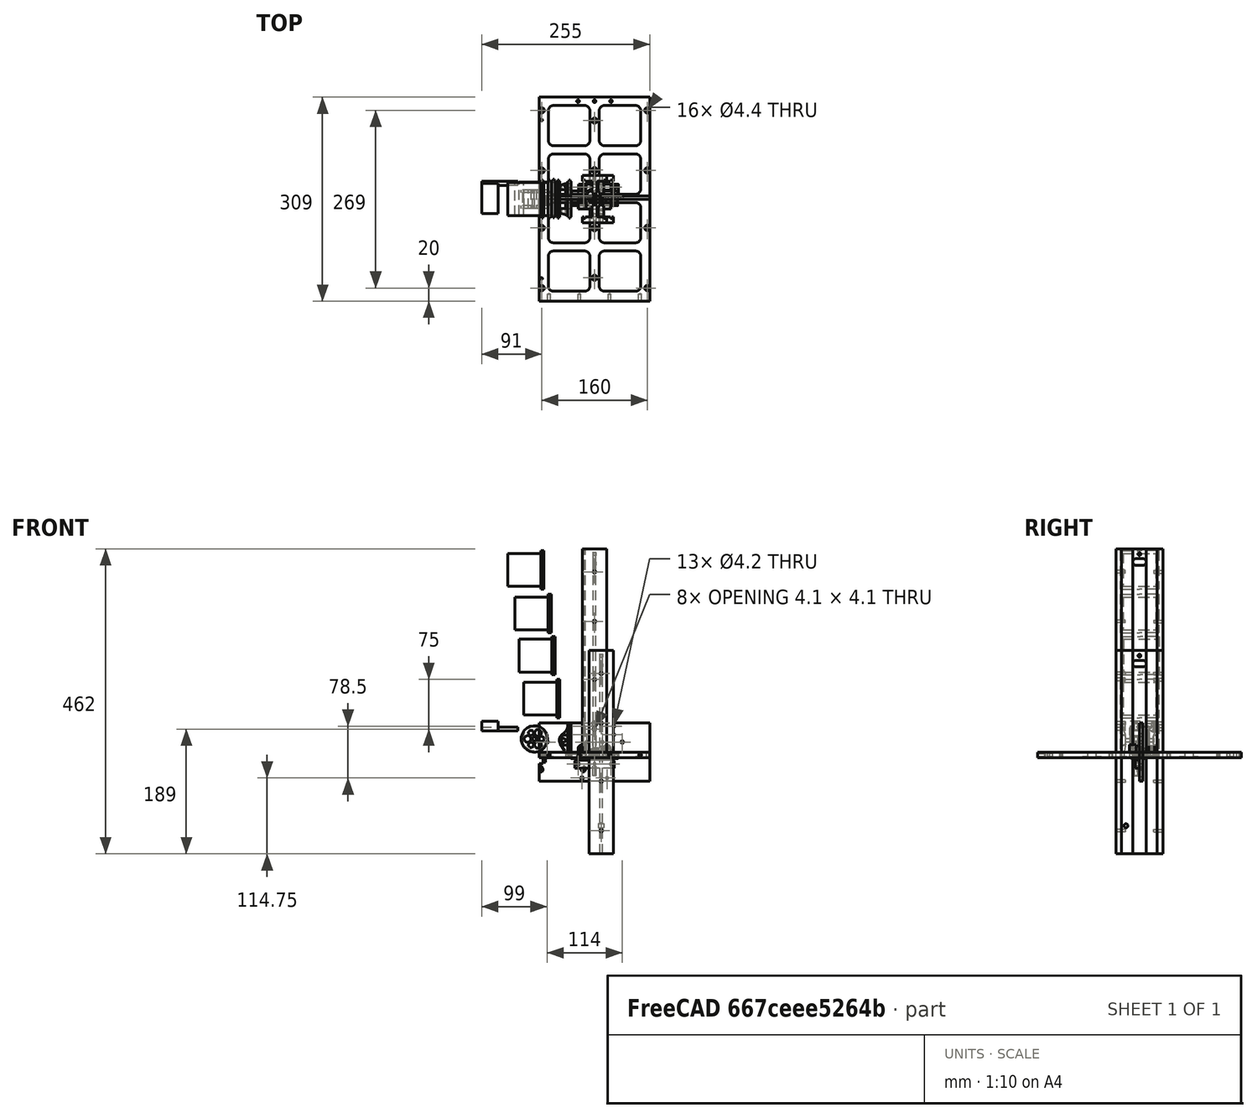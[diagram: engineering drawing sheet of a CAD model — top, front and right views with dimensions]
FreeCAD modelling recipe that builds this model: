
FCSTD DOCUMENT  (FreeCAD 0.22R35966 (Git))
Label: simulation
License: CreativeCommons Attribution-ShareAlike
LicenseURL: http://creativecommons.org/licenses/by-sa/4.0/
objects: PartDesign::CoordinateSystem×63, App::DocumentObjectGroupPython×56, Part::FeaturePython×21, App::Part×17, App::MaterialObjectPython×8, App::Link×7, App::DocumentObjectGroup×3, Part::Feature×3, App::TextDocument×3, Part::Line×3, App::FeaturePython×3
note: 90 computed .brp shape members not serialized (recipe doc carries the construction recipe); baked Part::Feature solids carry a one-line shape summary decoded from their .brp
EXTERNAL_REF file=pusher.FCStd obj=Part
EXTERNAL_REF file=pocketqube.FCStd obj=Part
EXTERNAL_REF file=pusher.FCStd obj=Part001
EXTERNAL_REF file=Stopper.FCStd obj=Part

FEATURE [Part::FeaturePython] rail_001  # a2plus imported part (geometry in sourceFile) (typed FeaturePython)
  Placement = pos=(6,0,0) rot=(0,0,1;0rad)
  a2p_Version = V0.1
  fixedPosition = false
  objectType = a2pPart
  sourceFile = ./rail.FCStd
  subassemblyImport = false
  timeLastImport = 1.5734e+09
  updateColors = true
FEATURE [App::Part] Part  label="Rail"
  Group = -> [rail_001]
  Origin = -> Origin
  Placement = pos=(10,0,154) rot=(0,0,-1;3.14159rad)
FEATURE [App::Link] Link003  label="PusherR"
  LinkPlacement = pos=(-27,-5.126e-06,43) rot=(0.57735,-0.57735,-0.57735;2.0944rad)
  LinkedObject = -> <external pusher.FCStd>#Part
  Placement = pos=(-27,-5.126e-06,43) rot=(0.57735,-0.57735,-0.57735;2.0944rad)
FEATURE [App::Link] Link  label="Satellite4R"
  LinkPlacement = pos=(-55,3.09944e-06,81) rot=(0,1,0;3.14159rad)
  LinkedObject = -> <external pocketqube.FCStd>#Part
  Placement = pos=(-55,3.09944e-06,81) rot=(0,1,0;3.14159rad)
FEATURE [App::Link] Link004  label="Satellite3R"
  LinkPlacement = pos=(-62,1.00001,146) rot=(0,1,0;3.14159rad)
  LinkedObject = -> <external pocketqube.FCStd>#Part
  Placement = pos=(-62,1.00001,146) rot=(0,1,0;3.14159rad)
FEATURE [App::Link] Link005  label="Satellite2R"
  LinkPlacement = pos=(-68,1.69277e-05,210) rot=(0,1,0;3.14159rad)
  LinkedObject = -> <external pocketqube.FCStd>#Part
  Placement = pos=(-68,1.69277e-05,210) rot=(0,1,0;3.14159rad)
FEATURE [App::Link] Link006  label="Satellite1R"
  LinkPlacement = pos=(-79,3.29018e-05,276) rot=(0,1,0;3.14159rad)
  LinkedObject = -> <external pocketqube.FCStd>#Part
  Placement = pos=(-79,3.29018e-05,276) rot=(0,1,0;3.14159rad)
FEATURE [Part::FeaturePython] Point001  # WARN: FeaturePython — macro-defined, semantics opaque (R4)
  Placement = pos=(-131.45,3.15905e-05,240) rot=(0,0,1;0rad)
  X = -131.45
  Y = 3.15905e-05
  Z = 240
FEATURE [Part::FeaturePython] Point002  # WARN: FeaturePython — macro-defined, semantics opaque (R4)
  Placement = pos=(-120.45,1.58548e-05,226) rot=(0,0,1;0rad)
  X = -120.45
  Y = 1.58548e-05
  Z = 226
FEATURE [App::Part] Part001  label="ContactPointSatellite1"
  Group = -> [Point001]
  Origin = -> Origin005
  Placement = pos=(-26,0,0) rot=(0,0,1;0rad)
FEATURE [App::Part] Part002  label="ContactPointSatellite2_1"
  Group = -> [Point002]
  Origin = -> Origin006
  Placement = pos=(-21,0,0) rot=(0,0,1;0rad)
FEATURE [Part::FeaturePython] Point  # WARN: FeaturePython — macro-defined, semantics opaque (R4)
  Placement = pos=(-120.45,1.58548e-05,176) rot=(0,0,1;0rad)
  X = -120.45
  Y = 1.58548e-05
  Z = 176
FEATURE [Part::FeaturePython] Point003  # WARN: FeaturePython — macro-defined, semantics opaque (R4)
  Placement = pos=(-114.45,1.00001,166) rot=(0,0,1;0rad)
  X = -114.45
  Y = 1.00001
  Z = 166
FEATURE [App::Part] Part003  label="ContactPointSatellite3_1"
  Group = -> [Point003]
  Origin = -> Origin007
  Placement = pos=(-13,0,0) rot=(0,0,1;0rad)
FEATURE [App::Part] Part004  label="ContactPointSatellite2_002"
  Group = -> [Point]
  Origin = -> Origin008
  Placement = pos=(-13,0,0) rot=(0,0,1;0rad)
FEATURE [Part::FeaturePython] Point004  # WARN: FeaturePython — macro-defined, semantics opaque (R4)
  Placement = pos=(-114.45,1.00001,116) rot=(0,0,1;0rad)
  X = -114.45
  Y = 1.00001
  Z = 116
FEATURE [Part::FeaturePython] Point005  # WARN: FeaturePython — macro-defined, semantics opaque (R4)
  Placement = pos=(-107.45,3.09944e-06,106) rot=(0,0,1;0rad)
  X = -107.45
  Y = 3.09944e-06
  Z = 106
FEATURE [App::Part] Part005
  Group = -> [Point004]
  Origin = -> Origin009
  Placement = pos=(-10,0,0) rot=(0,0,1;0rad)
FEATURE [App::Part] Part006
  Group = -> [Point005]
  Origin = -> Origin010
  Placement = pos=(-10,0,0) rot=(0,0,1;0rad)
FEATURE [App::DocumentObjectGroup] Group001  label="ContactPoints"
  Group = -> [Part001,Part002,Part003,Part004,Part005,Part006]
FEATURE [App::Link] Link007  label="Spool"
  LinkPlacement = pos=(-66,1.1146e-05,0) rot=(0,0,-1;1.5708rad)
  LinkedObject = -> <external pusher.FCStd>#Part001
  Placement = pos=(-66,1.1146e-05,0) rot=(0,0,-1;1.5708rad)
FEATURE [Part::Feature] y_plate_002  label="y-plate_002"
  shape: bbox 168 x 309 x 8.5 mm, 116 faces (baked)
FEATURE [App::Part] Part007  label="y-plate-up"
  Group = -> [y_plate_002]
  Origin = -> Origin011
  Placement = pos=(0,-88,132) rot=(1,0,0;1.5708rad)
FEATURE [Part::Feature] door_002
  shape: bbox 60 x 6 x 33.5 mm, 39 faces (baked)
FEATURE [App::Part] Part008  label="DoorLock"
  Group = -> [door_002]
  Origin = -> Origin012
  Placement = pos=(0,-104,304) rot=(0,0,1;3.14159rad)
FEATURE [Part::Feature] y_plate_001002  label="y-plate_003"
  shape: bbox 168 x 309 x 8.5 mm, 116 faces (baked)
FEATURE [App::Part] Part009  label="y-plate-down"
  Group = -> [y_plate_001002]
  Origin = -> Origin013
  Placement = pos=(0,122,142) rot=(0,0.707107,0.707107;3.14159rad)
FEATURE [Part::FeaturePython] hinge_002  # a2plus imported part (geometry in sourceFile) (typed FeaturePython)
  a2p_Version = V0.1
  fixedPosition = false
  objectType = a2pPart
  sourceFile = ./hinge.FCStd
  sourcePart = StatikHinge
  subassemblyImport = false
  timeLastImport = 1.58453e+09
  updateColors = true
FEATURE [App::Part] Part010  label="DoorHingeHolder"
  Group = -> [hinge_002]
  Origin = -> Origin014
  Placement = pos=(4.69e-14,160,299) rot=(0,-0.707107,0.707107;3.14159rad)
FEATURE [Part::FeaturePython] hinge_001  # a2plus imported part (geometry in sourceFile) (typed FeaturePython)
  a2p_Version = V0.1
  fixedPosition = false
  sourceFile = ./hinge.FCStd
  sourcePart = DoorHinge
  subassemblyImport = false
  timeLastImport = 1.57919e+09
  updateColors = true
FEATURE [App::Part] Part011  label="Hinge"
  Group = -> [hinge_001]
  Origin = -> Origin015
  Placement = pos=(1.93e-14,158,328) rot=(0,0.707107,-0.707107;3.14159rad)
FEATURE [Part::FeaturePython] door_001  # a2plus imported part (geometry in sourceFile) (typed FeaturePython)
  a2p_Version = V0.1
  fixedPosition = true
  sourceFile = ./door.FCStd
  sourcePart = Door
  subassemblyImport = false
  timeLastImport = 1.57919e+09
  updateColors = true
FEATURE [App::Part] Part012  label="Door"
  Group = -> [door_001]
  Origin = -> Origin016
  Placement = pos=(0,-5.8e-15,390) rot=(0,-0.707107,0.707107;3.14159rad)
FEATURE [Part::FeaturePython] door_003  # a2plus imported part (geometry in sourceFile) (typed FeaturePython)
  a2p_Version = V0.1
  fixedPosition = false
  sourceFile = ./door.FCStd
  sourcePart = BushingHolder
  subassemblyImport = false
  timeLastImport = 1.57919e+09
  updateColors = true
FEATURE [App::Part] Part013  label="DoorSlider"
  Group = -> [door_003]
  Origin = -> Origin017
  Placement = pos=(2.9e-15,-15,429) rot=(0,0,1;3.14159rad)
FEATURE [Part::FeaturePython] door_005  # a2plus imported part (geometry in sourceFile) (typed FeaturePython)
  a2p_Version = V0.1
  fixedPosition = false
  sourceFile = ./door.FCStd
  sourcePart = Slider
  subassemblyImport = false
  timeLastImport = 1.57919e+09
  updateColors = true
FEATURE [Part::FeaturePython] door_004  # a2plus imported part (geometry in sourceFile) (typed FeaturePython)
  a2p_Version = V0.1
  fixedPosition = false
  sourceFile = ./door.FCStd
  sourcePart = Pin
  subassemblyImport = false
  timeLastImport = 1.57919e+09
  updateColors = true
FEATURE [App::Part] Part014  label="DoorShaft"
  Group = -> [door_004]
  Origin = -> Origin018
  Placement = pos=(0,30,423) rot=(1,0,0;4.71239rad)
FEATURE [App::Part] Part015  label="DooShaftPusher"
  Group = -> [door_005]
  Origin = -> Origin019
  Placement = pos=(0,86,429) rot=(1,0,0;1.5708rad)
FEATURE [App::DocumentObjectGroupPython] MBD_animated_vectors  # scripted group (container) (typed FeaturePython)
FEATURE [App::DocumentObjectGroupPython] MBD_constitutive_laws  # scripted group (container) (typed FeaturePython)
FEATURE [App::DocumentObjectGroupPython] MBD_abstract_nodes  # scripted group (container) (typed FeaturePython)
FEATURE [App::DocumentObjectGroupPython] MBD_hydraulic_nodes  # scripted group (container) (typed FeaturePython)
FEATURE [App::DocumentObjectGroupPython] MBD_structural_static_nodes  # scripted group (container) (typed FeaturePython)
FEATURE [App::DocumentObjectGroupPython] MBD_beam_elements  # scripted group (container) (typed FeaturePython)
FEATURE [App::DocumentObjectGroupPython] MBD_genel_clamps  # scripted group (container) (typed FeaturePython)
FEATURE [App::DocumentObjectGroupPython] MBD_genel_elements  # scripted group (container) (typed FeaturePython)
  Group = -> [MBD_genel_clamps]
FEATURE [App::DocumentObjectGroupPython] MBD_gravity_elements  # scripted group (container) (typed FeaturePython)
FEATURE [App::DocumentObjectGroupPython] MBD_hydraulic_fluid_elements  # scripted group (container) (typed FeaturePython)
FEATURE [App::DocumentObjectGroupPython] MBD_hydraulic_elements  # scripted group (container) (typed FeaturePython)
  Group = -> [MBD_hydraulic_fluid_elements]
FEATURE [App::DocumentObjectGroupPython] MBD_angular_acceleration_joints  # scripted group (container) (typed FeaturePython)
FEATURE [App::DocumentObjectGroupPython] MBD_angular_velocity_joints  # scripted group (container) (typed FeaturePython)
FEATURE [App::DocumentObjectGroupPython] MBD_assembly_joints  # scripted group (container) (typed FeaturePython)
FEATURE [App::DocumentObjectGroupPython] MBD_coincidence_joints  # scripted group (container) (typed FeaturePython)
FEATURE [App::DocumentObjectGroupPython] MBD_cylindrical_joints  # scripted group (container) (typed FeaturePython)
FEATURE [App::DocumentObjectGroupPython] MBD_deformable_axial_joints  # scripted group (container) (typed FeaturePython)
FEATURE [App::DocumentObjectGroupPython] MBD_deformable_displacement_joints  # scripted group (container) (typed FeaturePython)
FEATURE [App::DocumentObjectGroupPython] MBD_deformable_hinge_joints  # scripted group (container) (typed FeaturePython)
FEATURE [App::DocumentObjectGroupPython] MBD_distance_joints  # scripted group (container) (typed FeaturePython)
FEATURE [App::DocumentObjectGroupPython] MBD_drive_hinge_joints  # scripted group (container) (typed FeaturePython)
FEATURE [App::DocumentObjectGroupPython] MBD_in_line_joints  # scripted group (container) (typed FeaturePython)
FEATURE [App::DocumentObjectGroupPython] MBD_linear_acceleration_joints  # scripted group (container) (typed FeaturePython)
FEATURE [App::DocumentObjectGroupPython] MBD_linear_velocity_joints  # scripted group (container) (typed FeaturePython)
FEATURE [App::DocumentObjectGroupPython] MBD_prismatic_joints  # scripted group (container) (typed FeaturePython)
FEATURE [App::DocumentObjectGroupPython] MBD_revolute_pin_joints  # scripted group (container) (typed FeaturePython)
FEATURE [App::DocumentObjectGroupPython] MBD_revolute_rotation_joints  # scripted group (container) (typed FeaturePython)
FEATURE [App::DocumentObjectGroupPython] MBD_shock_absorber_joints  # scripted group (container) (typed FeaturePython)
FEATURE [App::DocumentObjectGroupPython] MBD_spherical_hinge_joints  # scripted group (container) (typed FeaturePython)
FEATURE [App::DocumentObjectGroupPython] MBD_total_joints  # scripted group (container) (typed FeaturePython)
FEATURE [App::DocumentObjectGroupPython] MBD_total_pin_joints  # scripted group (container) (typed FeaturePython)
FEATURE [App::DocumentObjectGroupPython] MBD_viscous_body_joints  # scripted group (container) (typed FeaturePython)
FEATURE [App::DocumentObjectGroupPython] MBD_dummy_body_elements  # scripted group (container) (typed FeaturePython)
FEATURE [App::DocumentObjectGroupPython] MBD_gear_body_elements  # scripted group (container) (typed FeaturePython)
FEATURE [App::DocumentObjectGroupPython] MBD_static_body_elements  # scripted group (container) (typed FeaturePython)
FEATURE [App::DocumentObjectGroupPython] MBD_structural_couple_elements  # scripted group (container) (typed FeaturePython)
FEATURE [App::DocumentObjectGroupPython] MBD_scalar_functions  # scripted group (container) (typed FeaturePython)
FEATURE [App::TextDocument] ELEMENT_input_file
  Text = <blob: 59088 chars omitted>
FEATURE [App::TextDocument] ELEMENT_input_file_aux
  Text = begin: data;\n     problem: initial value;\n end: data;\n\n set: real XL = 0.0;\n set: real XU = 4.0;\n set: real dX = 0.01;\n\n begin: initial value;\n     initial time:   XL;\n     final time:     XU;\n     time step:      dX;\n     max iterations: 10;\n     tolerance:      1.e-6;\n     derivatives coefficient: auto;\n end: initial value;\n\n begin: control data;\n     abstract nodes: 2;\n     genels: 2;\n end: control data;\n\n     drive caller: 1, name, "drive: 1 ", cosine, 0.0, 3.1416, 7.0, half, 0.0;\n\n set: integer NoAbs_X = 1;\n set: integer NoAbs_Y = 2;\n set: integer GeClamp_NoAbs_X = 1;\n set: integer GeClamp_NoAbs_Y = 2;\n\n begin: nodes;\n     abstract: NoAbs_X, algebraic, value, XL;\n     abstract: NoAbs_Y, algebraic, value, model::drive(1, Time);\n end: nodes;\n\n set: [dof, X, NoAbs_X, abstract, algebraic];\n\n begin: elements;\n     genel: GeClamp_NoAbs_X,\n         clamp,\n         NoAbs_X, abstract,\n         string, "Time+XL";\n\n     genel: GeClamp_NoAbs_Y,\n         clamp,\n         NoAbs_Y, abstract,\n         string, "model::drive(1, Time)";\n\n end: elements;
FEATURE [App::DocumentObjectGroupPython] MBD_input_files  # scripted group (container) (typed FeaturePython)
  Group = -> [ELEMENT_input_file,ELEMENT_input_file_aux]
FEATURE [App::TextDocument] ELEMENT_variables
FEATURE [App::DocumentObjectGroupPython] MBD_user_defined_variables  # scripted group (container) (typed FeaturePython)
  Group = -> [ELEMENT_variables]
FEATURE [Part::Line] ELEMENT_cmx
  AttacherType = Attacher::AttachEngine3D
  X1 = -55
  X2 = -89.45
  Y1 = 3.09944e-06
  Y2 = 1.00001
  Z1 = 110
  Z2 = 121
FEATURE [Part::Line] ELEMENT_cmy
  AttacherType = Attacher::AttachEngine3D
  X1 = 0
  X2 = 0
  Y1 = 0
  Y2 = 0
  Z1 = 0
  Z2 = 1
FEATURE [Part::Line] ELEMENT_cmz
  AttacherType = Attacher::AttachEngine3D
  X1 = 0
  X2 = 0
  Y1 = 0
  Y2 = 0
  Z1 = 0
  Z2 = 1
FEATURE [PartDesign::CoordinateSystem] ELEMENT_ground
  AttacherType = Attacher::AttachEngine3D
FEATURE [App::DocumentObjectGroupPython] MBD_global_reference_frame  # scripted group (container) (typed FeaturePython)
  Group = -> [ELEMENT_cmx,ELEMENT_cmy,ELEMENT_cmz,ELEMENT_ground]
FEATURE [App::FeaturePython] ELEMENT_parameters  # WARN: FeaturePython — macro-defined, semantics opaque (R4)
  assembly_max_iterations = 1000
  default_orientation = 0
  derivatives_coefficient = auto
  derivatives_max_iterations = 100
  derivatives_tolerance = 0.0001
  final_time = 1
  initial_position_stiffness = 1
  initial_time = 0
  initial_velocity_stiffness = 1
  integration_max_iterations = 100
  model = 0
  modules_to_load = 0
  omega_rotates = 0
  output_data = 0
  output_meter = 10
  path_to_ELEMENT_executable = <userpath>/.local/share/FreeCAD/Mod/FreeCAD-motion-workbench-master/mbdyn-1.7.3-executables/LinuxExecutable/mbdyn
  print = 0
  skip_initial_joint_assembly = 0
  solver = 0
  time_step = 0.0001
  tolerance = 1e-06
  type_of_path_to_ELEMENT_executable = 0
  type_of_path_to_run_time_loadable_modules = 0
  type_of_working_directory = 0
  units = 0
FEATURE [App::FeaturePython] ELEMENT_animation  # WARN: FeaturePython — macro-defined, semantics opaque (R4)
  animationClicked = false
  assembled = false
  association0 = none
  association1 = none
  association2 = none
  association3 = none
  association4 = none
  association5 = none
  association6 = none
  association7 = none
  association8 = none
  association9 = none
  bodies_line_width = 1
  bodies_point_size = 4
  characteristic_length = 657
  continous = true
  current_time = 0
  current_time_step = 0
  follow_selected_object = false
  highlight_element = true
  objects_to_animate = 0
  speed = 0
  stop_at_time = 0
  stop_at_time_step = 0
  subAssembly = true
  transparency_when_assembled = 0
  transparency_when_exploded = 50
  zoon_when_contracted = 0.5
  zoon_when_expanded = 1
FEATURE [App::DocumentObjectGroupPython] MBD_simulation_parameters  # scripted group (container) (typed FeaturePython)
  Group = -> [ELEMENT_parameters,ELEMENT_animation]
FEATURE [Part::FeaturePython] ELEMENT_rigid_body_1  # WARN: FeaturePython — macro-defined, semantics opaque (R4)
  FirstAxisOfInertia = (1,0,0)
  Ixx = 20399.7
  Iyy = 18809.3
  Izz = 1937.59
  Placement = pos=(10,0,154) rot=(0,0,-1;3.14159rad)
  SecondAxisOfInertia = (0,1,0)
  ThirdAxisOfInertia = (0,0,1)
  absolute_center_of_mass_X = 7.1e-15
  absolute_center_of_mass_Y = -0.0154893
  absolute_center_of_mass_Z = 153.807
  base_entity = Part
  density = 7.9e-06
  ixx = 2.58225e+09
  iyy = 2.38093e+09
  izz = 2.45264e+08
  label = 1
  mass = 2.365
  material = Steel-Generic
  material_definition = 0
  material_object = ELEMENT_material_1
  node = 1
  relative_center_of_mass_X = 0
  relative_center_of_mass_Y = 0
  relative_center_of_mass_Z = 0
  type = rigid
  volume = 299367
FEATURE [App::MaterialObjectPython] ELEMENT_material_1  # material (typed FeaturePython)
  Category = 0
  Material = Density=7900.00 kg/m^3; Name=Steel-Generic
FEATURE [PartDesign::CoordinateSystem] ELEMENT_structural_dynamic_1
  AttacherType = Attacher::AttachEngine3D
  Placement = pos=(7.1e-15,-0.0154893,153.807) rot=(0,0,1;0rad)
  absolute_angular_velocity_X = 0
  absolute_angular_velocity_Y = 0
  absolute_angular_velocity_Z = 0
  absolute_orientation_matrix = 3, 0.0, 0.0, 1.0, 2, 0.0, 1.0, 0.0
  absolute_position_X = 7.1e-15
  absolute_position_Y = -0.0154893
  absolute_position_Z = 153.807
  absolute_velocity_X = 0
  absolute_velocity_Y = 0
  absolute_velocity_Z = 0
  base_entity = -> ELEMENT_rigid_body_1
  initial_conditions_reference_system_angular_velocity = 0
  initial_conditions_reference_system_velocity = 0
  label = 1
  offset_pitch = 0
  offset_reference_system_orientation = 0
  offset_reference_system_position = 0
  offset_roll = 0
  offset_x = 0
  offset_y = 0
  offset_yaw = 0
  offset_z = 0
  placement_method = 1
  plugin_variables = none
  position_reference_1 = -> ELEMENT_rigid_body_1
  type = dynamic
FEATURE [PartDesign::CoordinateSystem] ELEMENT_clamp_joint_1
  AttacherType = Attacher::AttachEngine3D
  Placement = pos=(7.1e-15,-0.0154893,153.807) rot=(0,0,1;0rad)
  absolute_orientation_matrix = 3, 0.0, 0.0, 1.0, 2, 0.0, 1.0, 0.0
  absolute_pin_position_X = 7.1e-15
  absolute_pin_position_Y = -0.0154893
  absolute_pin_position_Z = 153.807
  assembly_joint = false
  base_entity = -> ELEMENT_rigid_body_1
  driven_element = false
  driven_element_expression = Time <= 1.0
  group = 0
  joint = clamp
  joint_activation = 0
  label = 1
  plugin_variables = none
FEATURE [App::DocumentObjectGroupPython] MBD_clamp_joints  # scripted group (container) (typed FeaturePython)
  Group = -> [ELEMENT_clamp_joint_1]
FEATURE [Part::FeaturePython] ELEMENT_rigid_body_2  # WARN: FeaturePython — macro-defined, semantics opaque (R4)
  FirstAxisOfInertia = (1,0,-0.02)
  Ixx = 59.5536
  Iyy = 39.5563
  Izz = 23.3064
  Placement = pos=(-27,-5.126e-06,43) rot=(0.57735,-0.57735,-0.57735;2.0944rad)
  SecondAxisOfInertia = (0.02,0.05,1)
  ThirdAxisOfInertia = (0,1,-0.05)
  absolute_center_of_mass_X = -40.6441
  absolute_center_of_mass_Y = -0.426088
  absolute_center_of_mass_Z = 15.8381
  base_entity = Link003
  density = 7.9e-06
  ixx = 7.53844e+06
  iyy = 5.00713e+06
  izz = 2.95017e+06
  label = 2
  mass = 0.103087
  material = Steel-Generic
  material_definition = 0
  material_object = ELEMENT_material_2
  node = 2
  relative_center_of_mass_X = 0
  relative_center_of_mass_Y = 0
  relative_center_of_mass_Z = 0
  type = rigid
  volume = 13049
FEATURE [App::MaterialObjectPython] ELEMENT_material_2  # material (typed FeaturePython)
  Category = 0
  Material = Density=7900.00 kg/m^3; Name=Steel-Generic
FEATURE [PartDesign::CoordinateSystem] ELEMENT_structural_dynamic_2
  AttacherType = Attacher::AttachEngine3D
  Placement = pos=(-40.6441,-0.426088,15.8381) rot=(0,0,1;0rad)
  absolute_angular_velocity_X = 0
  absolute_angular_velocity_Y = 0
  absolute_angular_velocity_Z = 0
  absolute_orientation_matrix = 3, 0.0, 0.0, 1.0, 2, 0.0, 1.0, 0.0
  absolute_position_X = -40.6441
  absolute_position_Y = -0.426088
  absolute_position_Z = 15.8381
  absolute_velocity_X = 0
  absolute_velocity_Y = 0
  absolute_velocity_Z = 0
  base_entity = -> ELEMENT_rigid_body_2
  initial_conditions_reference_system_angular_velocity = 0
  initial_conditions_reference_system_velocity = 0
  label = 2
  offset_pitch = 0
  offset_reference_system_orientation = 0
  offset_reference_system_position = 0
  offset_roll = 0
  offset_x = 0
  offset_y = 0
  offset_yaw = 0
  offset_z = 0
  placement_method = 1
  plugin_variables = none
  position_reference_1 = -> ELEMENT_rigid_body_2
  type = dynamic
FEATURE [PartDesign::CoordinateSystem] ELEMENT_marker_2_1
  AttacherType = Attacher::AttachEngine3D
  Placement = pos=(-37.95,29,-6.99998) rot=(0,0,1;0rad)
  base_entity = -> ELEMENT_rigid_body_2
  label = 2
  offset_pitch = 0
  offset_reference_system_orientation = 0
  offset_reference_system_position = 0
  offset_roll = 0
  offset_x = 0
  offset_y = 0
  offset_yaw = 0
  offset_z = 0
  placement_method = 1
  position_reference_1 = -> ELEMENT_rigid_body_2 [Edge30]
FEATURE [PartDesign::CoordinateSystem] ELEMENT_slider_joint_2_3_4
  AttacherType = Attacher::AttachEngine3D
  Placement = pos=(-15,29,-2.84e-14) rot=(0,0,1;0rad)
  absolute_pin_position_X = -15
  absolute_pin_position_Y = 29
  absolute_pin_position_Z = -2.84e-14
  action_entity = -> ELEMENT_marker_2_1
  active = true
  angular_motion_expression = 0
  assembly_joint = false
  attachment_mode_1 = 0
  attachment_mode_2 = 0
  base_entity = -> ELEMENT_rigid_body_1
  direction = 0.0, 0.0, 1.0
  driven_element_expression = Time <= 1.0
  group = 0
  impose_angular_motion = 0
  impose_linear_motion = 0
  initial_angle = 0
  initial_angular_velocity = 0
  initial_distance = 143.831
  joint = slider
  joint_activation = 0
  label = 2_3_4
  linear_motion_expression = 0
  linear_stiffness = 10000
  linear_viscosity = 0
  offset_pitch = 0
  offset_reference_system_orientation = 0
  offset_reference_system_position = 0
  offset_roll = 0
  offset_x = 0
  offset_y = -0.25
  offset_yaw = 0
  offset_z = 0
  placement_method = 1
  plugin_variables = none
  position_reference_1 = -> ELEMENT_rigid_body_1 [Edge131]
  relative_line_position_X = -15
  relative_line_position_Y = 29.0155
  relative_line_position_Z = 0
  relative_offset_1_X = 0
  relative_offset_1_Y = 0
  relative_offset_1_Z = 0
  relative_offset_2_X = 0
  relative_offset_2_Y = 0
  relative_offset_2_Z = 0
  relative_offset_X = 2.69406
  relative_offset_Y = 29.4261
  relative_offset_Z = -22.8381
  relative_orientation = 3, 0.0, 0.0, 1.0, 2, 0.0, 1.0, 0.0
  relative_orientation_matrix_1 = 3, 0.0, 0.0, 1.0, 2, 0.0, 1.0, 0.0
  relative_orientation_matrix_2 = 3, 0.0, 0.0, 1.0, 2, 0.0, 1.0, 0.0
  rotation_axis = 0., 0., 1.
  rotational_stiffness = 40
  rotational_viscosity = 1e-05
FEATURE [PartDesign::CoordinateSystem] ELEMENT_structural_dummy_3
  AttacherType = Attacher::AttachEngine3D
  Placement = pos=(-3.73e-14,2.14e-14,308) rot=(0,0,1;0rad)
  absolute_position_X = -3.73e-14
  absolute_position_Y = 2.14e-14
  absolute_position_Z = 308
  base_entity = -> ELEMENT_rigid_body_1
  dummy_node_type = 0
  label = 3
  offset_pitch = 0
  offset_reference_system_orientation = 0
  offset_reference_system_position = 0
  offset_roll = 0
  offset_x = 0
  offset_y = 0
  offset_yaw = 0
  offset_z = 0
  placement_method = 1
  plugin_variables = "X_3_3": position in global direction 3 \n"XP_3_3": velocity in global direction 3
  position_reference_1 = -> ELEMENT_rigid_body_1 [Face17]
  relative_offset_X = -4.44e-14
  relative_offset_Y = 0.0154893
  relative_offset_Z = 154.193
  relative_orientation_matrix = 3, 0.0, 0.0, 1.0, 2, 0.0, 1.0, 0.0
  type = dummy
FEATURE [Part::FeaturePython] ELEMENT_rigid_body_4  # WARN: FeaturePython — macro-defined, semantics opaque (R4)
  FirstAxisOfInertia = (0,1,0)
  Ixx = 119.155
  Iyy = 118.532
  Izz = 107.581
  Placement = pos=(-55,3.09944e-06,81) rot=(0,1,0;3.14159rad)
  SecondAxisOfInertia = (0,0,1)
  ThirdAxisOfInertia = (1,0,0)
  absolute_center_of_mass_X = -79.3718
  absolute_center_of_mass_Y = 3.09944e-06
  absolute_center_of_mass_Z = 81
  base_entity = Link
  density = 1.77572e-06
  ixx = 6.7102e+07
  iyy = 6.67512e+07
  izz = 6.05841e+07
  label = 4
  mass = 0.25
  material = user-defined
  material_definition = 2
  material_object = ELEMENT_material_4
  node = 4
  relative_center_of_mass_X = 0
  relative_center_of_mass_Y = 0
  relative_center_of_mass_Z = 0
  type = rigid
  volume = 140788
FEATURE [App::MaterialObjectPython] ELEMENT_material_4  # material (typed FeaturePython)
  Category = 0
  Material = Density=7900.00 kg/m^3; Name=Steel-Generic
FEATURE [PartDesign::CoordinateSystem] ELEMENT_structural_dynamic_4
  AttacherType = Attacher::AttachEngine3D
  Placement = pos=(-79.3718,3.09944e-06,81) rot=(0,0,1;0rad)
  absolute_angular_velocity_X = 0
  absolute_angular_velocity_Y = 0
  absolute_angular_velocity_Z = 0
  absolute_orientation_matrix = 3, 0.0, 0.0, 1.0, 2, 0.0, 1.0, 0.0
  absolute_position_X = -79.3718
  absolute_position_Y = 3.09944e-06
  absolute_position_Z = 81
  absolute_velocity_X = 0
  absolute_velocity_Y = 0
  absolute_velocity_Z = 0
  base_entity = -> ELEMENT_rigid_body_4
  initial_conditions_reference_system_angular_velocity = 0
  initial_conditions_reference_system_velocity = 0
  label = 4
  offset_pitch = 0
  offset_reference_system_orientation = 0
  offset_reference_system_position = 0
  offset_roll = 0
  offset_x = 0
  offset_y = 0
  offset_yaw = 0
  offset_z = 0
  placement_method = 1
  plugin_variables = "X_3_4": position in global direction 3
  position_reference_1 = -> ELEMENT_rigid_body_4
  type = dynamic
FEATURE [PartDesign::CoordinateSystem] ELEMENT_marker_2_2
  AttacherType = Attacher::AttachEngine3D
  Placement = pos=(-39.5148,8.34466e-07,-6.99999) rot=(0,0,1;0rad)
  base_entity = -> ELEMENT_rigid_body_2
  label = 2
  offset_pitch = 0
  offset_reference_system_orientation = 0
  offset_reference_system_position = 0
  offset_roll = 0
  offset_x = 0
  offset_y = 0
  offset_yaw = 0
  offset_z = 0
  placement_method = 1
  position_reference_1 = -> ELEMENT_rigid_body_2 [Face4]
FEATURE [PartDesign::CoordinateSystem] ELEMENT_in_plane_joint_5
  AttacherType = Attacher::AttachEngine3D
  Placement = pos=(2.53e-14,7.94e-14,-2.84e-14) rot=(0,0,1;0rad)
  absolute_pin_position_X = 2.53e-14
  absolute_pin_position_Y = 7.94e-14
  absolute_pin_position_Z = -2.84e-14
  action_entity = -> ELEMENT_marker_2_2
  assembly_joint = false
  base_entity = -> ELEMENT_rigid_body_1
  driven_element = false
  driven_element_expression = Time <= 1.0
  joint = in plane
  joint_activation = 1
  label = 5
  offset_pitch = 0
  offset_reference_system_orientation = 0
  offset_reference_system_position = 0
  offset_roll = 0
  offset_x = 0
  offset_y = 0
  offset_yaw = 0
  offset_z = 0
  placement_method = 1
  plugin_variables = none
  position_reference_1 = -> ELEMENT_rigid_body_1 [Face19]
  relative_normal_direction = 0., 0., 1.
  relative_offset_X = 1.12923
  relative_offset_Y = 0.426089
  relative_offset_Z = -22.8381
  relative_plane_position_X = 1.82e-14
  relative_plane_position_Y = 0.0154893
  relative_plane_position_Z = -153.807
FEATURE [PartDesign::CoordinateSystem] ELEMENT_structural_dummy_5
  AttacherType = Attacher::AttachEngine3D
  Placement = pos=(-37.95,-5.126e-06,43) rot=(0,0,1;0rad)
  absolute_position_X = -37.95
  absolute_position_Y = -5.126e-06
  absolute_position_Z = 43
  base_entity = -> ELEMENT_rigid_body_2
  dummy_node_type = 0
  label = 5
  offset_pitch = 0
  offset_reference_system_orientation = 0
  offset_reference_system_position = 0
  offset_roll = 0
  offset_x = 0
  offset_y = 0
  offset_yaw = 0
  offset_z = 0
  placement_method = 1
  plugin_variables = "X_3_5": position in global direction 3 \n"XP_3_5": velocity in global direction 3
  position_reference_1 = -> ELEMENT_rigid_body_2 [Face3]
  relative_offset_X = 2.69405
  relative_offset_Y = 0.426083
  relative_offset_Z = 27.1619
  relative_orientation_matrix = 3, 0.0, 0.0, 1.0, 2, 0.0, 1.0, 0.0
  type = dummy
FEATURE [App::FeaturePython] ELEMENT_drive_1  # WARN: FeaturePython — macro-defined, semantics opaque (R4)
  a_final_time = 2
  a_initial_time = 1
  a_slope = 2
  amplitude = 7
  angular_vel = 3.1416
  const_coef = 9.807
  cubic_coef = 1
  d_final_time = 5
  d_initial_time = 4
  d_slope = -2
  expression = cosine, 0.0, 3.1416, 7.0, half, 0.0
  final_time = 4
  initial_time = 0
  initial_value = 0
  label = 1
  linear_coef = 1
  number_of_cycles = 2
  parabolic_coef = 1
  slope = 0.1
  slope_coef = 0.1
  step_value = 10
  steps_between_spikes = 10
  type = 1
FEATURE [App::DocumentObjectGroupPython] MBD_drives_and_drive_callers  # scripted group (container) (typed FeaturePython)
  Group = -> [ELEMENT_drive_1]
FEATURE [PartDesign::CoordinateSystem] ELEMENT_structural_force_1
  AttacherType = Attacher::AttachEngine3D
  Placement = pos=(-39.5148,8.34466e-07,-6.99999) rot=(0,0,1;0rad)
  base_entity = -> ELEMENT_rigid_body_2
  direction = 0.0, 0.0, 1.0
  driven_element_expression = Time <= 1.0
  element_activation = 0
  force = structural force
  force_value = drive_1(Time)
  label = 1
  offset_pitch = 0
  offset_reference_system_orientation = 0
  offset_reference_system_position = 0
  offset_roll = 0
  offset_x = 0
  offset_y = 0
  offset_yaw = 0
  offset_z = 0
  placement_method = 1
  position_reference_1 = -> ELEMENT_rigid_body_2 [Face4]
  relative_arm = 0.024079236764290426, 0.00042608808364651195, -0.01583810963787879
  type = 0
FEATURE [PartDesign::CoordinateSystem] ELEMENT_marker_1_1
  AttacherType = Attacher::AttachEngine3D
  Placement = pos=(-3.73e-14,2.14e-14,308) rot=(0,0,1;0rad)
  base_entity = -> ELEMENT_rigid_body_1
  label = 1
  offset_pitch = 0
  offset_reference_system_orientation = 0
  offset_reference_system_position = 0
  offset_roll = 0
  offset_x = 0
  offset_y = 0
  offset_yaw = 0
  offset_z = 0
  placement_method = 1
  position_reference_1 = -> ELEMENT_rigid_body_1 [Face17]
FEATURE [PartDesign::CoordinateSystem] ELEMENT_structural_internal_force_2
  AttacherType = Attacher::AttachEngine3D
  Placement = pos=(-37.95,-5.126e-06,43) rot=(1,0,0;3.14159rad)
  action_entity = -> ELEMENT_marker_1_1
  base_entity = -> ELEMENT_rigid_body_2
  contact_damping_activation_depth = 1e-06
  contact_damping_coefficient = 300
  contact_direction = 0
  contact_model = 1
  contact_offset = 0
  contact_stiffness_coefficient = 100000
  contact_stiffness_exponent = 1.2
  contact_type = 0
  direction = 0.0, -1.2246467991473532e-16, -1.0
  driven_element_expression = Time <= 1.0
  element_activation = 0
  force = structural internal force
  force_value = max(0, -Kc_2*(X_3_3 - X_3_5 + 0.0) - Cc_2*(XP_3_3 - XP_3_5))
  label = 2
  offset_pitch = 0
  offset_reference_system_orientation = 0
  offset_reference_system_position = 0
  offset_roll = 180
  offset_x = 0
  offset_y = 0
  offset_yaw = 0
  offset_z = 0
  placement_method = 1
  position_reference_1 = -> ELEMENT_rigid_body_2 [Face3]
  reference_node_1 = 5
  reference_node_2 = 3
  relative_arm_1 = 0.025644064041210078, 0.00042608212318202355, 0.03416189054866315
  relative_arm_2 = -4.4408920985006264e-17, 1.5489324329591213e-05, 0.15419324254671016
  type = 1
FEATURE [PartDesign::CoordinateSystem] ELEMENT_marker_4_1
  AttacherType = Attacher::AttachEngine3D
  Placement = pos=(-55,29,52) rot=(0,0,1;0rad)
  base_entity = -> ELEMENT_rigid_body_4
  label = 4
  offset_pitch = 0
  offset_reference_system_orientation = 0
  offset_reference_system_position = 0
  offset_roll = 0
  offset_x = 0
  offset_y = 0
  offset_yaw = 0
  offset_z = 0
  placement_method = 1
  position_reference_1 = -> ELEMENT_rigid_body_4 [Edge16]
FEATURE [PartDesign::CoordinateSystem] ELEMENT_slider_joint_6_7_8
  AttacherType = Attacher::AttachEngine3D
  Placement = pos=(-15,29,-2.84e-14) rot=(0,0,1;0rad)
  absolute_pin_position_X = -15
  absolute_pin_position_Y = 29
  absolute_pin_position_Z = -2.84e-14
  action_entity = -> ELEMENT_marker_4_1
  active = true
  angular_motion_expression = 0
  assembly_joint = false
  attachment_mode_1 = 0
  attachment_mode_2 = 0
  base_entity = -> ELEMENT_rigid_body_1
  direction = 0.0, 0.0, 1.0
  driven_element_expression = X_3_4< X_3_3
  group = 0
  impose_angular_motion = 0
  impose_linear_motion = 0
  initial_angle = 0
  initial_angular_velocity = 0
  initial_distance = 107.707
  joint = slider
  joint_activation = 3
  label = 6_7_8
  linear_motion_expression = 0
  linear_stiffness = 10000
  linear_viscosity = 0
  offset_pitch = 0
  offset_reference_system_orientation = 0
  offset_reference_system_position = 0
  offset_roll = 0
  offset_x = 0
  offset_y = -0.25
  offset_yaw = 0
  offset_z = 0
  placement_method = 1
  plugin_variables = none
  position_reference_1 = -> ELEMENT_rigid_body_1 [Edge131]
  relative_line_position_X = -15
  relative_line_position_Y = 29.0155
  relative_line_position_Z = 0
  relative_offset_1_X = 0
  relative_offset_1_Y = 0
  relative_offset_1_Z = 0
  relative_offset_2_X = 0
  relative_offset_2_Y = 0
  relative_offset_2_Z = 0
  relative_offset_X = 24.3718
  relative_offset_Y = 29
  relative_offset_Z = -29
  relative_orientation = 3, 0.0, 0.0, 1.0, 2, 0.0, 1.0, 0.0
  relative_orientation_matrix_1 = 3, 0.0, 0.0, 1.0, 2, 0.0, 1.0, 0.0
  relative_orientation_matrix_2 = 3, 0.0, 0.0, 1.0, 2, 0.0, 1.0, 0.0
  rotation_axis = 0., 0., 1.
  rotational_stiffness = 40
  rotational_viscosity = 1e-05
FEATURE [PartDesign::CoordinateSystem] ELEMENT_structural_dummy_6
  AttacherType = Attacher::AttachEngine3D
  Placement = pos=(-55,3.09944e-06,52) rot=(0,0,1;0rad)
  absolute_position_X = -55
  absolute_position_Y = 3.09944e-06
  absolute_position_Z = 52
  base_entity = -> ELEMENT_rigid_body_4
  dummy_node_type = 0
  label = 6
  offset_pitch = 0
  offset_reference_system_orientation = 0
  offset_reference_system_position = 0
  offset_roll = 0
  offset_x = 0
  offset_y = 0
  offset_yaw = 0
  offset_z = 0
  placement_method = 1
  plugin_variables = "X_3_6": position in global direction 3 \n"XP_3_6": velocity in global direction 3
  position_reference_1 = -> ELEMENT_rigid_body_4 [Edge20]
  relative_offset_X = 24.3718
  relative_offset_Y = 6e-16
  relative_offset_Z = -29
  relative_orientation_matrix = 3, 0.0, 0.0, 1.0, 2, 0.0, 1.0, 0.0
  type = dummy
FEATURE [PartDesign::CoordinateSystem] ELEMENT_marker_4_2
  AttacherType = Attacher::AttachEngine3D
  Placement = pos=(-55,3.09944e-06,52) rot=(0,-1,0;0.080285rad)
  base_entity = -> ELEMENT_rigid_body_4
  label = 4
  offset_pitch = 0
  offset_reference_system_orientation = 0
  offset_reference_system_position = 0
  offset_roll = 0
  offset_x = 0
  offset_y = 0
  offset_yaw = 0
  offset_z = 0
  placement_method = 1
  position_reference_1 = -> ELEMENT_rigid_body_4 [Edge20]
FEATURE [PartDesign::CoordinateSystem] ELEMENT_structural_internal_force_3
  AttacherType = Attacher::AttachEngine3D
  Placement = pos=(-37.95,-5.126e-06,43) rot=(0.999194,0,0.040132;3.14159rad)
  action_entity = -> ELEMENT_marker_4_2
  base_entity = -> ELEMENT_rigid_body_2
  contact_damping_activation_depth = 1e-06
  contact_damping_coefficient = 300
  contact_direction = 0
  contact_model = 1
  contact_offset = 0
  contact_stiffness_coefficient = 100000
  contact_stiffness_exponent = 1.2
  contact_type = 0
  direction = 0.08019892432885893, -1.2246467991473535e-16, -0.9967788784562475
  driven_element_expression = Time <= 1.0
  element_activation = 0
  force = structural internal force
  force_value = max(0, -Kc_3*(X_3_6 - X_3_5 + 0.0) - Cc_3*(XP_3_6 - XP_3_5))
  label = 3
  offset_pitch = -4.6
  offset_reference_system_orientation = 0
  offset_reference_system_position = 0
  offset_roll = 180
  offset_x = 0
  offset_y = 0
  offset_yaw = 0
  offset_z = 0
  placement_method = 1
  position_reference_1 = -> ELEMENT_rigid_body_2 [Face3]
  reference_node_1 = 5
  reference_node_2 = 6
  relative_arm_1 = 0.025644064041210078, 0.00042608212318202355, 0.03416189054866315
  relative_arm_2 = 0.024371817142041643, 6.179253580985891e-19, -0.029000002130651695
  type = 1
FEATURE [Part::FeaturePython] ELEMENT_rigid_body_7  # WARN: FeaturePython — macro-defined, semantics opaque (R4)
  FirstAxisOfInertia = (0,1,0)
  Ixx = 119.155
  Iyy = 118.532
  Izz = 107.581
  Placement = pos=(-62,1.00001,146) rot=(0,1,0;3.14159rad)
  SecondAxisOfInertia = (0,0,1)
  ThirdAxisOfInertia = (1,0,0)
  absolute_center_of_mass_X = -86.3719
  absolute_center_of_mass_Y = 1.00001
  absolute_center_of_mass_Z = 146
  base_entity = Link004
  density = 1.77572e-06
  ixx = 6.7102e+07
  iyy = 6.67512e+07
  izz = 6.05841e+07
  label = 7
  mass = 0.25
  material = user-defined
  material_definition = 2
  material_object = ELEMENT_material_7
  node = 7
  relative_center_of_mass_X = 0
  relative_center_of_mass_Y = 0
  relative_center_of_mass_Z = 0
  type = rigid
  volume = 140788
FEATURE [App::MaterialObjectPython] ELEMENT_material_7  # material (typed FeaturePython)
  Category = 0
  Material = Density=7900.00 kg/m^3; Name=Steel-Generic
FEATURE [PartDesign::CoordinateSystem] ELEMENT_structural_dynamic_7
  AttacherType = Attacher::AttachEngine3D
  Placement = pos=(-86.3719,1.00001,146) rot=(0,0,1;0rad)
  absolute_angular_velocity_X = 0
  absolute_angular_velocity_Y = 0
  absolute_angular_velocity_Z = 0
  absolute_orientation_matrix = 3, 0.0, 0.0, 1.0, 2, 0.0, 1.0, 0.0
  absolute_position_X = -86.3719
  absolute_position_Y = 1.00001
  absolute_position_Z = 146
  absolute_velocity_X = 0
  absolute_velocity_Y = 0
  absolute_velocity_Z = 0
  base_entity = -> ELEMENT_rigid_body_7
  initial_conditions_reference_system_angular_velocity = 0
  initial_conditions_reference_system_velocity = 0
  label = 7
  offset_pitch = 0
  offset_reference_system_orientation = 0
  offset_reference_system_position = 0
  offset_roll = 0
  offset_x = 0
  offset_y = 0
  offset_yaw = 0
  offset_z = 0
  placement_method = 1
  plugin_variables = "X_3_7": position in global direction 3
  position_reference_1 = -> ELEMENT_rigid_body_7
  type = dynamic
FEATURE [PartDesign::CoordinateSystem] ELEMENT_marker_7_1
  AttacherType = Attacher::AttachEngine3D
  Placement = pos=(-62,30,117) rot=(0,0,1;0rad)
  base_entity = -> ELEMENT_rigid_body_7
  label = 7
  offset_pitch = 0
  offset_reference_system_orientation = 0
  offset_reference_system_position = 0
  offset_roll = 0
  offset_x = 0
  offset_y = 0
  offset_yaw = 0
  offset_z = 0
  placement_method = 1
  position_reference_1 = -> ELEMENT_rigid_body_7 [Edge16]
FEATURE [PartDesign::CoordinateSystem] ELEMENT_slider_joint_9_10_11
  AttacherType = Attacher::AttachEngine3D
  Placement = pos=(-15,29,-2.84e-14) rot=(0,0,1;0rad)
  absolute_pin_position_X = -15
  absolute_pin_position_Y = 29
  absolute_pin_position_Z = -2.84e-14
  action_entity = -> ELEMENT_marker_7_1
  active = true
  angular_motion_expression = 0
  assembly_joint = false
  attachment_mode_1 = 0
  attachment_mode_2 = 0
  base_entity = -> ELEMENT_rigid_body_1
  direction = 0.0, 0.0, 1.0
  driven_element_expression = X_3_4< X_3_3
  group = 0
  impose_angular_motion = 0
  impose_linear_motion = 0
  initial_angle = 0
  initial_angular_velocity = 0
  initial_distance = 86.7299
  joint = slider
  joint_activation = 3
  label = 9_10_11
  linear_motion_expression = 0
  linear_stiffness = 10000
  linear_viscosity = 0
  offset_pitch = 0
  offset_reference_system_orientation = 0
  offset_reference_system_position = 0
  offset_roll = 0
  offset_x = 0
  offset_y = -0.25
  offset_yaw = 0
  offset_z = 0
  placement_method = 1
  plugin_variables = none
  position_reference_1 = -> ELEMENT_rigid_body_1 [Edge131]
  relative_line_position_X = -15
  relative_line_position_Y = 29.0155
  relative_line_position_Z = 0
  relative_offset_1_X = 0
  relative_offset_1_Y = 0
  relative_offset_1_Z = 0
  relative_offset_2_X = 0
  relative_offset_2_Y = 0
  relative_offset_2_Z = 0
  relative_offset_X = 24.3718
  relative_offset_Y = 29
  relative_offset_Z = -29
  relative_orientation = 3, 0.0, 0.0, 1.0, 2, 0.0, 1.0, 0.0
  relative_orientation_matrix_1 = 3, 0.0, 0.0, 1.0, 2, 0.0, 1.0, 0.0
  relative_orientation_matrix_2 = 3, 0.0, 0.0, 1.0, 2, 0.0, 1.0, 0.0
  rotation_axis = 0., 0., 1.
  rotational_stiffness = 40
  rotational_viscosity = 1e-05
FEATURE [PartDesign::CoordinateSystem] ELEMENT_structural_dummy_8
  AttacherType = Attacher::AttachEngine3D
  Placement = pos=(-55,3.09944e-06,110) rot=(0,0,1;0rad)
  absolute_position_X = -55
  absolute_position_Y = 3.09944e-06
  absolute_position_Z = 110
  base_entity = -> ELEMENT_rigid_body_4
  dummy_node_type = 0
  label = 8
  offset_pitch = 0
  offset_reference_system_orientation = 0
  offset_reference_system_position = 0
  offset_roll = 0
  offset_x = 0
  offset_y = 0
  offset_yaw = 0
  offset_z = 0
  placement_method = 1
  plugin_variables = "X_3_8": position in global direction 3 \n"XP_3_8": velocity in global direction 3
  position_reference_1 = -> ELEMENT_rigid_body_4 [Edge15]
  relative_offset_X = 24.3718
  relative_offset_Y = 6e-16
  relative_offset_Z = 29
  relative_orientation_matrix = 3, 0.0, 0.0, 1.0, 2, 0.0, 1.0, 0.0
  type = dummy
FEATURE [PartDesign::CoordinateSystem] ELEMENT_structural_dummy_9
  AttacherType = Attacher::AttachEngine3D
  Placement = pos=(-62,1.00001,117) rot=(0,0,1;0rad)
  absolute_position_X = -62
  absolute_position_Y = 1.00001
  absolute_position_Z = 117
  base_entity = -> ELEMENT_rigid_body_7
  dummy_node_type = 0
  label = 9
  offset_pitch = 0
  offset_reference_system_orientation = 0
  offset_reference_system_position = 0
  offset_roll = 0
  offset_x = 0
  offset_y = 0
  offset_yaw = 0
  offset_z = 0
  placement_method = 1
  plugin_variables = "X_3_9": position in global direction 3 \n"XP_3_9": velocity in global direction 3
  position_reference_1 = -> ELEMENT_rigid_body_7 [Edge20]
  relative_offset_X = 24.3718
  relative_offset_Y = 1.8e-15
  relative_offset_Z = -29
  relative_orientation_matrix = 3, 0.0, 0.0, 1.0, 2, 0.0, 1.0, 0.0
  type = dummy
FEATURE [PartDesign::CoordinateSystem] ELEMENT_marker_7_2
  AttacherType = Attacher::AttachEngine3D
  Placement = pos=(-62,1.00001,117) rot=(0,-1,0;0.080285rad)
  base_entity = -> ELEMENT_rigid_body_7
  label = 7
  offset_pitch = 0
  offset_reference_system_orientation = 0
  offset_reference_system_position = 0
  offset_roll = 0
  offset_x = 0
  offset_y = 0
  offset_yaw = 0
  offset_z = 0
  placement_method = 1
  position_reference_1 = -> ELEMENT_rigid_body_7 [Edge20]
FEATURE [PartDesign::CoordinateSystem] ELEMENT_structural_internal_force_4
  AttacherType = Attacher::AttachEngine3D
  Placement = pos=(-55,3.09944e-06,110) rot=(0.999194,0,0.040132;3.14159rad)
  action_entity = -> ELEMENT_marker_7_2
  base_entity = -> ELEMENT_rigid_body_4
  contact_damping_activation_depth = 1e-06
  contact_damping_coefficient = 300
  contact_direction = 0
  contact_model = 1
  contact_offset = 0
  contact_stiffness_coefficient = 100000
  contact_stiffness_exponent = 1.2
  contact_type = 0
  direction = 0.08019892432885893, -1.2246467991473535e-16, -0.9967788784562475
  driven_element_expression = Time <= 1.0
  element_activation = 0
  force = structural internal force
  force_value = max(0, -Kc_4*(X_3_9 - X_3_8 + 0.0) - Cc_4*(XP_3_9 - XP_3_8))
  label = 4
  offset_pitch = -4.6
  offset_reference_system_orientation = 0
  offset_reference_system_position = 0
  offset_roll = 180
  offset_x = 0
  offset_y = 0
  offset_yaw = 0
  offset_z = 0
  placement_method = 1
  position_reference_1 = -> ELEMENT_rigid_body_4 [Edge15]
  reference_node_1 = 8
  reference_node_2 = 9
  relative_arm_1 = 0.06437180281637728, -3.0994324169841495e-09, 0.028999998109301785
  relative_arm_2 = 0.0243718171420402, 1.7763568394002505e-18, -0.029000002130652902
  type = 1
FEATURE [Part::FeaturePython] ELEMENT_rigid_body_10  # WARN: FeaturePython — macro-defined, semantics opaque (R4)
  FirstAxisOfInertia = (0,1,0)
  Ixx = 119.155
  Iyy = 118.532
  Izz = 107.581
  Placement = pos=(-68,1.69277e-05,210) rot=(0,1,0;3.14159rad)
  SecondAxisOfInertia = (0,0,1)
  ThirdAxisOfInertia = (1,0,0)
  absolute_center_of_mass_X = -92.3718
  absolute_center_of_mass_Y = 1.69277e-05
  absolute_center_of_mass_Z = 210
  base_entity = Link005
  density = 1.77572e-06
  ixx = 6.7102e+07
  iyy = 6.67512e+07
  izz = 6.05841e+07
  label = 10
  mass = 0.25
  material = user-defined
  material_definition = 2
  material_object = ELEMENT_material_10
  node = 10
  relative_center_of_mass_X = 0
  relative_center_of_mass_Y = 0
  relative_center_of_mass_Z = 0
  type = rigid
  volume = 140788
FEATURE [App::MaterialObjectPython] ELEMENT_material_10  # material (typed FeaturePython)
  Category = 0
  Material = Density=7900.00 kg/m^3; Name=Steel-Generic
FEATURE [PartDesign::CoordinateSystem] ELEMENT_structural_dynamic_10
  AttacherType = Attacher::AttachEngine3D
  Placement = pos=(-92.3718,1.69277e-05,210) rot=(0,0,1;0rad)
  absolute_angular_velocity_X = 0
  absolute_angular_velocity_Y = 0
  absolute_angular_velocity_Z = 0
  absolute_orientation_matrix = 3, 0.0, 0.0, 1.0, 2, 0.0, 1.0, 0.0
  absolute_position_X = -92.3718
  absolute_position_Y = 1.69277e-05
  absolute_position_Z = 210
  absolute_velocity_X = 0
  absolute_velocity_Y = 0
  absolute_velocity_Z = 0
  base_entity = -> ELEMENT_rigid_body_10
  initial_conditions_reference_system_angular_velocity = 0
  initial_conditions_reference_system_velocity = 0
  label = 10
  offset_pitch = 0
  offset_reference_system_orientation = 0
  offset_reference_system_position = 0
  offset_roll = 0
  offset_x = 0
  offset_y = 0
  offset_yaw = 0
  offset_z = 0
  placement_method = 1
  plugin_variables = "X_3_10": position in global direction 3
  position_reference_1 = -> ELEMENT_rigid_body_10
  type = dynamic
FEATURE [PartDesign::CoordinateSystem] ELEMENT_marker_10_1
  AttacherType = Attacher::AttachEngine3D
  Placement = pos=(-68,29,181) rot=(0,0,1;0rad)
  base_entity = -> ELEMENT_rigid_body_10
  label = 10
  offset_pitch = 0
  offset_reference_system_orientation = 0
  offset_reference_system_position = 0
  offset_roll = 0
  offset_x = 0
  offset_y = 0
  offset_yaw = 0
  offset_z = 0
  placement_method = 1
  position_reference_1 = -> ELEMENT_rigid_body_10 [Edge16]
FEATURE [PartDesign::CoordinateSystem] ELEMENT_slider_joint_12_13_14
  AttacherType = Attacher::AttachEngine3D
  Placement = pos=(-15,29,-2.84e-14) rot=(0,0,1;0rad)
  absolute_pin_position_X = -15
  absolute_pin_position_Y = 29
  absolute_pin_position_Z = -2.84e-14
  action_entity = -> ELEMENT_marker_10_1
  active = true
  angular_motion_expression = 0
  assembly_joint = false
  attachment_mode_1 = 0
  attachment_mode_2 = 0
  base_entity = -> ELEMENT_rigid_body_1
  direction = 0.0, 0.0, 1.0
  driven_element_expression = X_3_10< X_3_3
  group = 0
  impose_angular_motion = 0
  impose_linear_motion = 0
  initial_angle = 0
  initial_angular_velocity = 0
  initial_distance = 108.121
  joint = slider
  joint_activation = 3
  label = 12_13_14
  linear_motion_expression = 0
  linear_stiffness = 10000
  linear_viscosity = 0
  offset_pitch = 0
  offset_reference_system_orientation = 0
  offset_reference_system_position = 0
  offset_roll = 0
  offset_x = 0
  offset_y = -0.25
  offset_yaw = 0
  offset_z = 0
  placement_method = 1
  plugin_variables = none
  position_reference_1 = -> ELEMENT_rigid_body_1 [Edge131]
  relative_line_position_X = -15
  relative_line_position_Y = 29.0155
  relative_line_position_Z = 0
  relative_offset_1_X = 0
  relative_offset_1_Y = 0
  relative_offset_1_Z = 0
  relative_offset_2_X = 0
  relative_offset_2_Y = 0
  relative_offset_2_Z = 0
  relative_offset_X = 24.3718
  relative_offset_Y = 29
  relative_offset_Z = -29
  relative_orientation = 3, 0.0, 0.0, 1.0, 2, 0.0, 1.0, 0.0
  relative_orientation_matrix_1 = 3, 0.0, 0.0, 1.0, 2, 0.0, 1.0, 0.0
  relative_orientation_matrix_2 = 3, 0.0, 0.0, 1.0, 2, 0.0, 1.0, 0.0
  rotation_axis = 0., 0., 1.
  rotational_stiffness = 40
  rotational_viscosity = 1e-05
FEATURE [PartDesign::CoordinateSystem] ELEMENT_structural_dummy_11
  AttacherType = Attacher::AttachEngine3D
  Placement = pos=(-62,1.00001,175) rot=(0,0,1;0rad)
  absolute_position_X = -62
  absolute_position_Y = 1.00001
  absolute_position_Z = 175
  base_entity = -> ELEMENT_rigid_body_7
  dummy_node_type = 0
  label = 11
  offset_pitch = 0
  offset_reference_system_orientation = 0
  offset_reference_system_position = 0
  offset_roll = 0
  offset_x = 0
  offset_y = 0
  offset_yaw = 0
  offset_z = 0
  placement_method = 1
  plugin_variables = "X_3_11": position in global direction 3 \n"XP_3_11": velocity in global direction 3
  position_reference_1 = -> ELEMENT_rigid_body_7 [Edge15]
  relative_offset_X = 24.3718
  relative_offset_Y = 1.8e-15
  relative_offset_Z = 29
  relative_orientation_matrix = 3, 0.0, 0.0, 1.0, 2, 0.0, 1.0, 0.0
  type = dummy
FEATURE [PartDesign::CoordinateSystem] ELEMENT_structural_dummy_12
  AttacherType = Attacher::AttachEngine3D
  Placement = pos=(-68,1.69277e-05,181) rot=(0,0,1;0rad)
  absolute_position_X = -68
  absolute_position_Y = 1.69277e-05
  absolute_position_Z = 181
  base_entity = -> ELEMENT_rigid_body_10
  dummy_node_type = 0
  label = 12
  offset_pitch = 0
  offset_reference_system_orientation = 0
  offset_reference_system_position = 0
  offset_roll = 0
  offset_x = 0
  offset_y = 0
  offset_yaw = 0
  offset_z = 0
  placement_method = 1
  plugin_variables = "X_3_12": position in global direction 3 \n"XP_3_12": velocity in global direction 3
  position_reference_1 = -> ELEMENT_rigid_body_10 [Edge20]
  relative_offset_X = 24.3718
  relative_offset_Y = -8.55e-14
  relative_offset_Z = -29
  relative_orientation_matrix = 3, 0.0, 0.0, 1.0, 2, 0.0, 1.0, 0.0
  type = dummy
FEATURE [PartDesign::CoordinateSystem] ELEMENT_marker_10_3
  AttacherType = Attacher::AttachEngine3D
  Placement = pos=(-68,1.69277e-05,181) rot=(0,-1,0;0.080285rad)
  base_entity = -> ELEMENT_rigid_body_10
  label = 10
  offset_pitch = 0
  offset_reference_system_orientation = 0
  offset_reference_system_position = 0
  offset_roll = 0
  offset_x = 0
  offset_y = 0
  offset_yaw = 0
  offset_z = 0
  placement_method = 1
  position_reference_1 = -> ELEMENT_rigid_body_10 [Edge20]
FEATURE [PartDesign::CoordinateSystem] ELEMENT_structural_internal_force_5
  AttacherType = Attacher::AttachEngine3D
  Placement = pos=(-62,1.00001,175) rot=(0.999194,0,0.040132;3.14159rad)
  action_entity = -> ELEMENT_marker_10_3
  base_entity = -> ELEMENT_rigid_body_7
  contact_damping_activation_depth = 1e-06
  contact_damping_coefficient = 300
  contact_direction = 0
  contact_model = 1
  contact_offset = 0
  contact_stiffness_coefficient = 100000
  contact_stiffness_exponent = 1.2
  contact_type = 0
  direction = 0.08019892432885893, -1.2246467991473535e-16, -0.9967788784562475
  driven_element_expression = Time <= 1.0
  element_activation = 0
  force = structural internal force
  force_value = max(0, -Kc_5*(X_3_12 - X_3_11 + 0.0) - Cc_5*(XP_3_12 - XP_3_11))
  label = 5
  offset_pitch = -4.6
  offset_reference_system_orientation = 0
  offset_reference_system_position = 0
  offset_roll = 180
  offset_x = 0
  offset_y = 0
  offset_yaw = 0
  offset_z = 0
  placement_method = 1
  position_reference_1 = -> ELEMENT_rigid_body_7 [Edge15]
  reference_node_1 = 11
  reference_node_2 = 12
  relative_arm_1 = 0.07137185240744319, -0.0010000129938025416, 0.028999995738693884
  relative_arm_2 = 0.024371817142039988, -8.54883011440228e-17, -0.029000002130653114
  type = 1
FEATURE [Part::FeaturePython] ELEMENT_rigid_body_13  # WARN: FeaturePython — macro-defined, semantics opaque (R4)
  FirstAxisOfInertia = (0,1,0)
  Ixx = 119.155
  Iyy = 118.532
  Izz = 107.581
  Placement = pos=(-79,3.29018e-05,276) rot=(0,1,0;3.14159rad)
  SecondAxisOfInertia = (0,0,1)
  ThirdAxisOfInertia = (1,0,0)
  absolute_center_of_mass_X = -103.372
  absolute_center_of_mass_Y = 3.29018e-05
  absolute_center_of_mass_Z = 276
  base_entity = Link006
  density = 1.77572e-06
  ixx = 6.7102e+07
  iyy = 6.67512e+07
  izz = 6.05841e+07
  label = 13
  mass = 0.25
  material = user-defined
  material_definition = 2
  material_object = ELEMENT_material_13
  node = 13
  relative_center_of_mass_X = 0
  relative_center_of_mass_Y = 0
  relative_center_of_mass_Z = 0
  type = rigid
  volume = 140788
FEATURE [App::MaterialObjectPython] ELEMENT_material_13  # material (typed FeaturePython)
  Category = 0
  Material = Density=7900.00 kg/m^3; Name=Steel-Generic
FEATURE [PartDesign::CoordinateSystem] ELEMENT_structural_dynamic_13
  AttacherType = Attacher::AttachEngine3D
  Placement = pos=(-103.372,3.29018e-05,276) rot=(0,0,1;0rad)
  absolute_angular_velocity_X = 0
  absolute_angular_velocity_Y = 0
  absolute_angular_velocity_Z = 0
  absolute_orientation_matrix = 3, 0.0, 0.0, 1.0, 2, 0.0, 1.0, 0.0
  absolute_position_X = -103.372
  absolute_position_Y = 3.29018e-05
  absolute_position_Z = 276
  absolute_velocity_X = 0
  absolute_velocity_Y = 0
  absolute_velocity_Z = 0
  base_entity = -> ELEMENT_rigid_body_13
  initial_conditions_reference_system_angular_velocity = 0
  initial_conditions_reference_system_velocity = 0
  label = 13
  offset_pitch = 0
  offset_reference_system_orientation = 0
  offset_reference_system_position = 0
  offset_roll = 0
  offset_x = 0
  offset_y = 0
  offset_yaw = 0
  offset_z = 0
  placement_method = 1
  plugin_variables = "X_3_13": position in global direction 3
  position_reference_1 = -> ELEMENT_rigid_body_13
  type = dynamic
FEATURE [PartDesign::CoordinateSystem] ELEMENT_marker_13_1
  AttacherType = Attacher::AttachEngine3D
  Placement = pos=(-79,29,247) rot=(0,0,1;0rad)
  base_entity = -> ELEMENT_rigid_body_13
  label = 13
  offset_pitch = 0
  offset_reference_system_orientation = 0
  offset_reference_system_position = 0
  offset_roll = 0
  offset_x = 0
  offset_y = 0
  offset_yaw = 0
  offset_z = 0
  placement_method = 1
  position_reference_1 = -> ELEMENT_rigid_body_13 [Edge16]
FEATURE [PartDesign::CoordinateSystem] ELEMENT_slider_joint_15_16_17
  AttacherType = Attacher::AttachEngine3D
  Placement = pos=(-15,29,-2.84e-14) rot=(0,0,1;0rad)
  absolute_pin_position_X = -15
  absolute_pin_position_Y = 29
  absolute_pin_position_Z = -2.84e-14
  action_entity = -> ELEMENT_marker_13_1
  active = true
  angular_motion_expression = 0
  assembly_joint = false
  attachment_mode_1 = 0
  attachment_mode_2 = 0
  base_entity = -> ELEMENT_rigid_body_1
  direction = 0.0, 0.0, 1.0
  driven_element_expression = X_3_13< X_3_3
  group = 0
  impose_angular_motion = 0
  impose_linear_motion = 0
  initial_angle = 0
  initial_angular_velocity = 0
  initial_distance = 160.053
  joint = slider
  joint_activation = 3
  label = 15_16_17
  linear_motion_expression = 0
  linear_stiffness = 10000
  linear_viscosity = 0
  offset_pitch = 0
  offset_reference_system_orientation = 0
  offset_reference_system_position = 0
  offset_roll = 0
  offset_x = 0
  offset_y = -0.25
  offset_yaw = 0
  offset_z = 0
  placement_method = 1
  plugin_variables = none
  position_reference_1 = -> ELEMENT_rigid_body_1 [Edge131]
  relative_line_position_X = -15
  relative_line_position_Y = 29.0155
  relative_line_position_Z = 0
  relative_offset_1_X = 0
  relative_offset_1_Y = 0
  relative_offset_1_Z = 0
  relative_offset_2_X = 0
  relative_offset_2_Y = 0
  relative_offset_2_Z = 0
  relative_offset_X = 24.3718
  relative_offset_Y = 29
  relative_offset_Z = -29
  relative_orientation = 3, 0.0, 0.0, 1.0, 2, 0.0, 1.0, 0.0
  relative_orientation_matrix_1 = 3, 0.0, 0.0, 1.0, 2, 0.0, 1.0, 0.0
  relative_orientation_matrix_2 = 3, 0.0, 0.0, 1.0, 2, 0.0, 1.0, 0.0
  rotation_axis = 0., 0., 1.
  rotational_stiffness = 40
  rotational_viscosity = 1e-05
FEATURE [App::DocumentObjectGroupPython] MBD_slider_joints  # scripted group (container) (typed FeaturePython)
  Group = -> [ELEMENT_slider_joint_2_3_4,ELEMENT_slider_joint_6_7_8,ELEMENT_slider_joint_9_10_11,ELEMENT_slider_joint_12_13_14,ELEMENT_slider_joint_15_16_17]
FEATURE [PartDesign::CoordinateSystem] ELEMENT_structural_dummy_14
  AttacherType = Attacher::AttachEngine3D
  Placement = pos=(-68,1.69277e-05,239) rot=(0,0,1;0rad)
  absolute_position_X = -68
  absolute_position_Y = 1.69277e-05
  absolute_position_Z = 239
  base_entity = -> ELEMENT_rigid_body_10
  dummy_node_type = 0
  label = 14
  offset_pitch = 0
  offset_reference_system_orientation = 0
  offset_reference_system_position = 0
  offset_roll = 0
  offset_x = 0
  offset_y = 0
  offset_yaw = 0
  offset_z = 0
  placement_method = 1
  plugin_variables = "X_3_14": position in global direction 3 \n"XP_3_14": velocity in global direction 3
  position_reference_1 = -> ELEMENT_rigid_body_10 [Edge15]
  relative_offset_X = 24.3718
  relative_offset_Y = -8.55e-14
  relative_offset_Z = 29
  relative_orientation_matrix = 3, 0.0, 0.0, 1.0, 2, 0.0, 1.0, 0.0
  type = dummy
FEATURE [PartDesign::CoordinateSystem] ELEMENT_structural_dummy_15
  AttacherType = Attacher::AttachEngine3D
  Placement = pos=(-79,3.29018e-05,247) rot=(0,0,1;0rad)
  absolute_position_X = -79
  absolute_position_Y = 3.29018e-05
  absolute_position_Z = 247
  base_entity = -> ELEMENT_rigid_body_13
  dummy_node_type = 0
  label = 15
  offset_pitch = 0
  offset_reference_system_orientation = 0
  offset_reference_system_position = 0
  offset_roll = 0
  offset_x = 0
  offset_y = 0
  offset_yaw = 0
  offset_z = 0
  placement_method = 1
  plugin_variables = "X_3_15": position in global direction 3 \n"XP_3_15": velocity in global direction 3
  position_reference_1 = -> ELEMENT_rigid_body_13 [Edge20]
  relative_offset_X = 24.3718
  relative_offset_Y = -1e-16
  relative_offset_Z = -29
  relative_orientation_matrix = 3, 0.0, 0.0, 1.0, 2, 0.0, 1.0, 0.0
  type = dummy
FEATURE [PartDesign::CoordinateSystem] ELEMENT_marker_13_2
  AttacherType = Attacher::AttachEngine3D
  Placement = pos=(-79,3.29018e-05,247) rot=(0,-1,0;0.080285rad)
  base_entity = -> ELEMENT_rigid_body_13
  label = 13
  offset_pitch = 0
  offset_reference_system_orientation = 0
  offset_reference_system_position = 0
  offset_roll = 0
  offset_x = 0
  offset_y = 0
  offset_yaw = 0
  offset_z = 0
  placement_method = 1
  position_reference_1 = -> ELEMENT_rigid_body_13 [Edge20]
FEATURE [PartDesign::CoordinateSystem] ELEMENT_structural_internal_force_6
  AttacherType = Attacher::AttachEngine3D
  Placement = pos=(-68,1.69277e-05,239) rot=(0.999194,0,0.040132;3.14159rad)
  action_entity = -> ELEMENT_marker_13_2
  base_entity = -> ELEMENT_rigid_body_10
  contact_damping_activation_depth = 1e-06
  contact_damping_coefficient = 300
  contact_direction = 0
  contact_model = 1
  contact_offset = 0
  contact_stiffness_coefficient = 100000
  contact_stiffness_exponent = 1.2
  contact_type = 0
  direction = 0.08019892432885893, -1.2246467991473535e-16, -0.9967788784562475
  driven_element_expression = Time <= 1.0
  element_activation = 0
  force = structural internal force
  force_value = max(0, -Kc_6*(X_3_15 - X_3_14 + 0.0) - Cc_6*(XP_3_15 - XP_3_14))
  label = 6
  offset_pitch = -4.6
  offset_reference_system_orientation = 0
  offset_reference_system_position = 0
  offset_roll = 180
  offset_x = 0
  offset_y = 0
  offset_yaw = 0
  offset_z = 0
  placement_method = 1
  position_reference_1 = -> ELEMENT_rigid_body_10 [Edge15]
  reference_node_1 = 14
  reference_node_2 = 15
  relative_arm_1 = 0.07737180663107619, -1.6927703722766622e-08, 0.029000010997482548
  relative_arm_2 = 0.0243718171420404, -5.1872297689853354e-20, -0.029000002130652746
  type = 1
FEATURE [PartDesign::CoordinateSystem] ELEMENT_structural_dummy_16
  AttacherType = Attacher::AttachEngine3D
  Placement = pos=(-95.45,1.69277e-05,235) rot=(0,0,1;0rad)
  absolute_position_X = -95.45
  absolute_position_Y = 1.69277e-05
  absolute_position_Z = 235
  base_entity = -> ELEMENT_rigid_body_10
  dummy_node_type = 0
  label = 16
  offset_pitch = 0
  offset_reference_system_orientation = 0
  offset_reference_system_position = 0
  offset_roll = 0
  offset_x = 0
  offset_y = 0
  offset_yaw = 0
  offset_z = 0
  placement_method = 1
  plugin_variables = "X_3_16": position in global direction 3 \n"XP_3_16": velocity in global direction 3
  position_reference_1 = -> ELEMENT_rigid_body_10 [Face15]
  relative_offset_X = -3.07818
  relative_offset_Y = 9.7e-15
  relative_offset_Z = 25
  relative_orientation_matrix = 3, 0.0, 0.0, 1.0, 2, 0.0, 1.0, 0.0
  type = dummy
FEATURE [PartDesign::CoordinateSystem] ELEMENT_structural_dummy_17
  AttacherType = Attacher::AttachEngine3D
  Placement = pos=(-141.45,3.29018e-05,251) rot=(0,0,1;0rad)
  absolute_position_X = -141.45
  absolute_position_Y = 3.29018e-05
  absolute_position_Z = 251
  base_entity = -> ELEMENT_rigid_body_13
  dummy_node_type = 0
  label = 17
  offset_pitch = 0
  offset_reference_system_orientation = 0
  offset_reference_system_position = 0
  offset_roll = 0
  offset_x = -10
  offset_y = 0
  offset_yaw = 0
  offset_z = 0
  placement_method = 1
  plugin_variables = "X_3_17": position in global direction 3 \n"XP_3_17": velocity in global direction 3
  position_reference_1 = -> ELEMENT_rigid_body_13 [Edge54]
  relative_offset_X = -38.0782
  relative_offset_Y = -3.6e-15
  relative_offset_Z = -25
  relative_orientation_matrix = 3, 0.0, 0.0, 1.0, 2, 0.0, 1.0, 0.0
  type = dummy
FEATURE [PartDesign::CoordinateSystem] ELEMENT_marker_13_3
  AttacherType = Attacher::AttachEngine3D
  Placement = pos=(-79,3.29018e-05,305) rot=(0,0,1;0rad)
  base_entity = -> ELEMENT_rigid_body_13
  label = 13
  offset_pitch = 0
  offset_reference_system_orientation = 0
  offset_reference_system_position = 0
  offset_roll = 0
  offset_x = 0
  offset_y = 0
  offset_yaw = 0
  offset_z = 0
  placement_method = 1
  position_reference_1 = -> ELEMENT_rigid_body_13 [Edge15]
FEATURE [PartDesign::CoordinateSystem] ELEMENT_in_plane_joint_18
  AttacherType = Attacher::AttachEngine3D
  Placement = pos=(-3.73e-14,2.14e-14,308) rot=(0,0,1;0rad)
  absolute_pin_position_X = -3.73e-14
  absolute_pin_position_Y = 2.14e-14
  absolute_pin_position_Z = 308
  action_entity = -> ELEMENT_marker_13_3
  assembly_joint = false
  base_entity = -> ELEMENT_rigid_body_1
  driven_element = false
  driven_element_expression = Time < 0.5
  joint = in plane
  joint_activation = 3
  label = 18
  offset_pitch = 0
  offset_reference_system_orientation = 0
  offset_reference_system_position = 0
  offset_roll = 0
  offset_x = 0
  offset_y = 0
  offset_yaw = 0
  offset_z = 0
  placement_method = 1
  plugin_variables = none
  position_reference_1 = -> ELEMENT_rigid_body_1 [Face17]
  relative_normal_direction = 0., 0., 1.
  relative_offset_X = 24.3718
  relative_offset_Y = -1e-16
  relative_offset_Z = 29
  relative_plane_position_X = -4.44e-14
  relative_plane_position_Y = 0.0154893
  relative_plane_position_Z = 154.193
FEATURE [App::DocumentObjectGroupPython] MBD_in_plane_joints  # scripted group (container) (typed FeaturePython)
  Group = -> [ELEMENT_in_plane_joint_5,ELEMENT_in_plane_joint_18]
FEATURE [PartDesign::CoordinateSystem] ELEMENT_marker_13_4
  AttacherType = Attacher::AttachEngine3D
  Placement = pos=(-131.45,3.29018e-05,251) rot=(0,-1,0;0.080285rad)
  base_entity = -> ELEMENT_rigid_body_13
  label = 13
  offset_pitch = 0
  offset_reference_system_orientation = 0
  offset_reference_system_position = 0
  offset_roll = 0
  offset_x = 0
  offset_y = 0
  offset_yaw = 0
  offset_z = 0
  placement_method = 1
  position_reference_1 = -> ELEMENT_rigid_body_13 [Edge54]
FEATURE [PartDesign::CoordinateSystem] ELEMENT_structural_internal_force_7
  AttacherType = Attacher::AttachEngine3D
  Placement = pos=(-120.45,1.69277e-05,235) rot=(0.999194,0,0.040132;3.14159rad)
  action_entity = -> ELEMENT_marker_13_4
  base_entity = -> ELEMENT_rigid_body_10
  contact_damping_activation_depth = 1e-06
  contact_damping_coefficient = 300
  contact_direction = 0
  contact_model = 1
  contact_offset = 0
  contact_stiffness_coefficient = 100000
  contact_stiffness_exponent = 1.2
  contact_type = 0
  direction = 0.08019892432885893, -1.2246467991473535e-16, -0.9967788784562475
  driven_element_expression = Time <= 1.0
  element_activation = 0
  force = structural internal force
  force_value = max(0, -Kc_7*(X_3_17 - X_3_16 + 0.0) - Cc_7*(XP_3_17 - XP_3_16))
  label = 7
  offset_pitch = -4.6
  offset_reference_system_orientation = 0
  offset_reference_system_position = 0
  offset_roll = 180
  offset_x = 0
  offset_y = 0
  offset_yaw = 0
  offset_z = 0
  placement_method = 1
  position_reference_1 = -> ELEMENT_rigid_body_10 [Edge50]
  reference_node_1 = 16
  reference_node_2 = 17
  relative_arm_1 = 0.0249218062813851, -1.6927703544847335e-08, 0.025000015582809426
  relative_arm_2 = -0.028078182508268185, -3.646578481883433e-18, -0.024999997545326638
  type = 1
FEATURE [PartDesign::CoordinateSystem] ELEMENT_structural_dummy_18
  AttacherType = Attacher::AttachEngine3D
  Placement = pos=(-89.45,1.00001,171) rot=(0,0,1;0rad)
  absolute_position_X = -89.45
  absolute_position_Y = 1.00001
  absolute_position_Z = 171
  base_entity = -> ELEMENT_rigid_body_7
  dummy_node_type = 0
  label = 18
  offset_pitch = 0
  offset_reference_system_orientation = 0
  offset_reference_system_position = 0
  offset_roll = 0
  offset_x = 0
  offset_y = 0
  offset_yaw = 0
  offset_z = 0
  placement_method = 1
  plugin_variables = "X_3_18": position in global direction 3 \n"XP_3_18": velocity in global direction 3
  position_reference_1 = -> ELEMENT_rigid_body_7 [Face15]
  relative_offset_X = -3.07818
  relative_offset_Y = -4e-16
  relative_offset_Z = 25
  relative_orientation_matrix = 3, 0.0, 0.0, 1.0, 2, 0.0, 1.0, 0.0
  type = dummy
FEATURE [PartDesign::CoordinateSystem] ELEMENT_structural_dummy_19
  AttacherType = Attacher::AttachEngine3D
  Placement = pos=(-130.45,1.69277e-05,185) rot=(0,0,1;0rad)
  absolute_position_X = -130.45
  absolute_position_Y = 1.69277e-05
  absolute_position_Z = 185
  base_entity = -> ELEMENT_rigid_body_10
  dummy_node_type = 0
  label = 19
  offset_pitch = 0
  offset_reference_system_orientation = 0
  offset_reference_system_position = 0
  offset_roll = 0
  offset_x = -10
  offset_y = 0
  offset_yaw = 0
  offset_z = 0
  placement_method = 1
  plugin_variables = "X_3_19": position in global direction 3 \n"XP_3_19": velocity in global direction 3
  position_reference_1 = -> ELEMENT_rigid_body_10 [Edge54]
  relative_offset_X = -38.0782
  relative_offset_Y = 9.22e-14
  relative_offset_Z = -25
  relative_orientation_matrix = 3, 0.0, 0.0, 1.0, 2, 0.0, 1.0, 0.0
  type = dummy
FEATURE [PartDesign::CoordinateSystem] ELEMENT_marker_10_004
  AttacherType = Attacher::AttachEngine3D
  Placement = pos=(-120.45,1.69277e-05,185) rot=(0,-1,0;0.080285rad)
  base_entity = -> ELEMENT_rigid_body_10
  label = 10
  offset_pitch = 0
  offset_reference_system_orientation = 0
  offset_reference_system_position = 0
  offset_roll = 0
  offset_x = 0
  offset_y = 0
  offset_yaw = 0
  offset_z = 0
  placement_method = 1
  position_reference_1 = -> ELEMENT_rigid_body_10 [Edge54]
FEATURE [PartDesign::CoordinateSystem] ELEMENT_structural_internal_force_8
  AttacherType = Attacher::AttachEngine3D
  Placement = pos=(-114.45,1.00001,171) rot=(0.999194,0,0.040132;3.14159rad)
  action_entity = -> ELEMENT_marker_10_004
  base_entity = -> ELEMENT_rigid_body_7
  contact_damping_activation_depth = 1e-06
  contact_damping_coefficient = 300
  contact_direction = 0
  contact_model = 1
  contact_offset = 0
  contact_stiffness_coefficient = 100000
  contact_stiffness_exponent = 1.2
  contact_type = 0
  direction = 0.08019892432885893, -1.2246467991473535e-16, -0.9967788784562475
  driven_element_expression = Time <= 1.0
  element_activation = 0
  force = structural internal force
  force_value = max(0, -Kc_8*(X_3_19 - X_3_18 + 0.0) - Cc_8*(XP_3_19 - XP_3_18))
  label = 8
  offset_pitch = -4.6
  offset_reference_system_orientation = 0
  offset_reference_system_position = 0
  offset_roll = 180
  offset_x = 0
  offset_y = 0
  offset_yaw = 0
  offset_z = 0
  placement_method = 1
  position_reference_1 = -> ELEMENT_rigid_body_7 [Edge50]
  reference_node_1 = 18
  reference_node_2 = 19
  relative_arm_1 = 0.01892185205775212, -0.0010000129938025442, 0.025000000324020392
  relative_arm_2 = -0.028078182508268556, 9.219010374972997e-17, -0.02499999754532624
  type = 1
FEATURE [PartDesign::CoordinateSystem] ELEMENT_structural_dummy_20
  AttacherType = Attacher::AttachEngine3D
  Placement = pos=(-82.45,3.09944e-06,106) rot=(0,0,1;0rad)
  absolute_position_X = -82.45
  absolute_position_Y = 3.09944e-06
  absolute_position_Z = 106
  base_entity = -> ELEMENT_rigid_body_4
  dummy_node_type = 0
  label = 20
  offset_pitch = 0
  offset_reference_system_orientation = 0
  offset_reference_system_position = 0
  offset_roll = 0
  offset_x = 0
  offset_y = 0
  offset_yaw = 0
  offset_z = 0
  placement_method = 1
  plugin_variables = "X_3_20": position in global direction 3 \n"XP_3_20": velocity in global direction 3
  position_reference_1 = -> ELEMENT_rigid_body_4 [Face15]
  relative_offset_X = -3.07818
  relative_offset_Y = -1.5e-15
  relative_offset_Z = 25
  relative_orientation_matrix = 3, 0.0, 0.0, 1.0, 2, 0.0, 1.0, 0.0
  type = dummy
FEATURE [PartDesign::CoordinateSystem] ELEMENT_structural_dummy_21
  AttacherType = Attacher::AttachEngine3D
  Placement = pos=(-124.45,1.00001,121) rot=(0,0,1;0rad)
  absolute_position_X = -124.45
  absolute_position_Y = 1.00001
  absolute_position_Z = 121
  base_entity = -> ELEMENT_rigid_body_7
  dummy_node_type = 0
  label = 21
  offset_pitch = 0
  offset_reference_system_orientation = 0
  offset_reference_system_position = 0
  offset_roll = 0
  offset_x = -10
  offset_y = 0
  offset_yaw = 0
  offset_z = 0
  placement_method = 1
  plugin_variables = "X_3_21": position in global direction 3 \n"XP_3_21": velocity in global direction 3
  position_reference_1 = -> ELEMENT_rigid_body_7 [Edge54]
  relative_offset_X = -38.0782
  relative_offset_Y = -1.8e-15
  relative_offset_Z = -25
  relative_orientation_matrix = 3, 0.0, 0.0, 1.0, 2, 0.0, 1.0, 0.0
  type = dummy
FEATURE [PartDesign::CoordinateSystem] ELEMENT_marker_7_3
  AttacherType = Attacher::AttachEngine3D
  Placement = pos=(-114.45,1.00001,121) rot=(0,-1,0;0.080285rad)
  base_entity = -> ELEMENT_rigid_body_7
  label = 7
  offset_pitch = 0
  offset_reference_system_orientation = 0
  offset_reference_system_position = 0
  offset_roll = 0
  offset_x = 0
  offset_y = 0
  offset_yaw = 0
  offset_z = 0
  placement_method = 1
  position_reference_1 = -> ELEMENT_rigid_body_7 [Edge54]
FEATURE [PartDesign::CoordinateSystem] ELEMENT_structural_internal_force_9
  AttacherType = Attacher::AttachEngine3D
  Placement = pos=(-107.45,3.09944e-06,106) rot=(0.999194,0,0.040132;3.14159rad)
  action_entity = -> ELEMENT_marker_7_3
  base_entity = -> ELEMENT_rigid_body_4
  contact_damping_activation_depth = 1e-06
  contact_damping_coefficient = 300
  contact_direction = 0
  contact_model = 1
  contact_offset = 0
  contact_stiffness_coefficient = 100000
  contact_stiffness_exponent = 1.2
  contact_type = 0
  direction = 0.08019892432885893, -1.2246467991473535e-16, -0.9967788784562475
  driven_element_expression = Time <= 1.0
  element_activation = 0
  force = structural internal force
  force_value = max(0, -Kc_9*(X_3_21 - X_3_20 + 0.0) - Cc_9*(XP_3_21 - XP_3_20))
  label = 9
  offset_pitch = -4.6
  offset_reference_system_orientation = 0
  offset_reference_system_position = 0
  offset_roll = 180
  offset_x = 0
  offset_y = 0
  offset_yaw = 0
  offset_z = 0
  placement_method = 1
  position_reference_1 = -> ELEMENT_rigid_body_4 [Edge50]
  reference_node_1 = 20
  reference_node_2 = 21
  relative_arm_1 = 0.011921802466686416, -3.099432422082214e-09, 0.025000002694625677
  relative_arm_2 = -0.028078182508268355, -1.7763568394002505e-18, -0.024999997545326422
  type = 1
FEATURE [Part::FeaturePython] ELEMENT_rigid_body_22  # WARN: FeaturePython — macro-defined, semantics opaque (R4)
  FirstAxisOfInertia = (0,1,0)
  Ixx = 31.5673
  Iyy = 26.6938
  Izz = 26.6938
  Placement = pos=(-66,1.1146e-05,0) rot=(0,0,-1;1.5708rad)
  SecondAxisOfInertia = (-0.03,0,1)
  ThirdAxisOfInertia = (1,0,0.03)
  absolute_center_of_mass_X = -91
  absolute_center_of_mass_Y = 1.53607e-05
  absolute_center_of_mass_Z = 20
  base_entity = Link007
  density = 7.9e-06
  ixx = 3.99586e+06
  iyy = 3.37896e+06
  izz = 3.37896e+06
  label = 22
  mass = 0.148514
  material = Steel-Generic
  material_definition = 0
  material_object = ELEMENT_material_22
  node = 22
  relative_center_of_mass_X = 0
  relative_center_of_mass_Y = 0
  relative_center_of_mass_Z = 0
  type = rigid
  volume = 18799.3
FEATURE [App::MaterialObjectPython] ELEMENT_material_22  # material (typed FeaturePython)
  Category = 0
  Material = Density=7900.00 kg/m^3; Name=Steel-Generic
FEATURE [PartDesign::CoordinateSystem] ELEMENT_structural_dynamic_22
  AttacherType = Attacher::AttachEngine3D
  Placement = pos=(-91,1.53607e-05,20) rot=(0.999775,-0.014993,0.014993;1.57102rad)
  absolute_angular_velocity_X = 0
  absolute_angular_velocity_Y = 0
  absolute_angular_velocity_Z = 0
  absolute_orientation_matrix = 3, -3.469446951953614e-18, -1.0, 1.1102230246251565e-16, 2, -0.029986509105671, 1.1102230246251565e-16, 0.9995503035223667
  absolute_position_X = -91
  absolute_position_Y = 1.53607e-05
  absolute_position_Z = 20
  absolute_velocity_X = 0
  absolute_velocity_Y = 0
  absolute_velocity_Z = 0
  base_entity = -> ELEMENT_rigid_body_22
  initial_conditions_reference_system_angular_velocity = 0
  initial_conditions_reference_system_velocity = 0
  label = 22
  offset_pitch = 0
  offset_reference_system_orientation = 0
  offset_reference_system_position = 0
  offset_roll = 0
  offset_x = 0
  offset_y = 0
  offset_yaw = 0
  offset_z = 0
  placement_method = 0
  plugin_variables = none
  type = dynamic
FEATURE [PartDesign::CoordinateSystem] ELEMENT_marker_2_3
  AttacherType = Attacher::AttachEngine3D
  Placement = pos=(-47,14.3486,18) rot=(1,0,0;1.5708rad)
  base_entity = -> ELEMENT_rigid_body_2
  label = 2
  offset_pitch = 0
  offset_reference_system_orientation = 0
  offset_reference_system_position = 0
  offset_roll = 0
  offset_x = 0
  offset_y = 0
  offset_yaw = 0
  offset_z = 0
  orientation_reference_1 = -> ELEMENT_rigid_body_2 [Edge142]
  placement_method = 1
  position_reference_1 = -> ELEMENT_rigid_body_2 [Edge57]
FEATURE [PartDesign::CoordinateSystem] ELEMENT_hinge_joint_19_20
  AttacherType = Attacher::AttachEngine3D
  Placement = pos=(-91,14,20) rot=(1,0,0;1.5708rad)
  absolute_pin_position_X = -91
  absolute_pin_position_Y = 14
  absolute_pin_position_Z = 20
  action_entity = -> ELEMENT_marker_2_3
  angular_motion_expression = 0
  assembly_joint = false
  base_entity = -> ELEMENT_rigid_body_22
  driven_element_expression = Time <= 1.0
  hinge_direction = -1.6858739623363112e-07, -0.9999999999999858, 0.0
  impose_angular_motion = 0
  initial_angle = 0
  initial_angular_velocity = 0
  joint = hinge
  joint_activation = 0
  label = 19_20
  offset_pitch = 0
  offset_reference_system_orientation = 0
  offset_reference_system_position = 0
  offset_roll = 0
  offset_x = 0
  offset_y = 0
  offset_yaw = 0
  offset_z = 0
  orientation_reference_1 = -> ELEMENT_rigid_body_22 [Face10]
  placement_method = 1
  plugin_variables = none
  position_reference_1 = -> ELEMENT_rigid_body_22 [Edge10]
  rel_rot_orientation_1 = 3, 0.0, 1.0, 0.0, 2, guess
  rel_rot_orientation_2 = 3, -1.6858739623363112e-07, -0.9999999999999858, 0.0, 2, guess
  relative_pin_orientation_matrix_1 = 3, -1.6851158307883782e-07, 5.055347270243555e-09, 0.9999999999999858, 2, 0.029986509105671, 0.9995503035223667, 2.2202169160847328e-16
  relative_pin_orientation_matrix_2 = 3, -1.6858739623363112e-07, -0.9999999999999858, 0.0, 2, 0.0, 0.0, 1.0
  relative_pin_position_1_X = 2.35916e-06
  relative_pin_position_1_Y = -7.07748e-08
  relative_pin_position_1_Z = -14
  relative_pin_position_2_X = -50.3559
  relative_pin_position_2_Y = 14.4261
  relative_pin_position_2_Z = 4.16189
  rotation_axis = 0., 0., 1.
  rotational_stiffness = 40
  rotational_viscosity = 1e-05
FEATURE [App::DocumentObjectGroupPython] MBD_hinge_joints  # scripted group (container) (typed FeaturePython)
  Group = -> [ELEMENT_hinge_joint_19_20]
FEATURE [App::DocumentObjectGroupPython] MBD_joint_elements  # scripted group (container) (typed FeaturePython)
  Group = -> [MBD_angular_acceleration_joints,MBD_angular_velocity_joints,MBD_assembly_joints,MBD_clamp_joints,MBD_coincidence_joints,MBD_cylindrical_joints,MBD_deformable_axial_joints,MBD_deformable_displacement_joints,MBD_deformable_hinge_joints,MBD_distance_joints,MBD_drive_hinge_joints,MBD_in_line_joints,MBD_in_plane_joints,MBD_linear_acceleration_joints,MBD_linear_velocity_joints,MBD_prismatic_joints,+9 more]
FEATURE [App::Link] Link008  label="Stopper"
  LinkPlacement = pos=(-116,24,35) rot=(0.57735,-0.57735,-0.57735;2.0944rad)
  LinkedObject = -> <external Stopper.FCStd>#Part
  Placement = pos=(-116,24,35) rot=(0.57735,-0.57735,-0.57735;2.0944rad)
FEATURE [App::DocumentObjectGroup] Group002  label="PARTS"
  Group = -> [Link007,Part,Link003,Link,Link004,Link005,Link006,Part007,Part008,Part009,Part010,Part011,Part012,Part013,Part014,Part015,Link008]
FEATURE [App::DocumentObjectGroup] Group  label="CAD"
  Group = -> [Group001,Group002]
FEATURE [Part::FeaturePython] ELEMENT_rigid_body_23  # WARN: FeaturePython — macro-defined, semantics opaque (R4)
  FirstAxisOfInertia = (0.06,0.02,1)
  Ixx = 39.559
  Iyy = 30.6235
  Izz = 13.7268
  Placement = pos=(-116,24,35) rot=(0.57735,-0.57735,-0.57735;2.0944rad)
  SecondAxisOfInertia = (0.97,-0.24,-0.06)
  ThirdAxisOfInertia = (0.24,0.97,-0.04)
  absolute_center_of_mass_X = -157.182
  absolute_center_of_mass_Y = 2.82038
  absolute_center_of_mass_Z = 38.9614
  base_entity = Link008
  density = 7.9e-06
  ixx = 5.00746e+06
  iyy = 3.87639e+06
  izz = 1.73756e+06
  label = 23
  mass = 0.139794
  material = Steel-Generic
  material_definition = 0
  material_object = ELEMENT_material_23
  node = 23
  relative_center_of_mass_X = 0
  relative_center_of_mass_Y = 0
  relative_center_of_mass_Z = 0
  type = rigid
  volume = 17695.4
FEATURE [App::DocumentObjectGroupPython] MBD_rigid_body_elements  # scripted group (container) (typed FeaturePython)
  Group = -> [ELEMENT_rigid_body_1,ELEMENT_rigid_body_2,ELEMENT_rigid_body_4,ELEMENT_rigid_body_7,ELEMENT_rigid_body_10,ELEMENT_rigid_body_13,ELEMENT_rigid_body_22,ELEMENT_rigid_body_23]
FEATURE [App::Part] MBD_body_elements
  Group = -> [MBD_dummy_body_elements,MBD_rigid_body_elements,MBD_gear_body_elements,MBD_static_body_elements,ELEMENT_rigid_body_1,ELEMENT_rigid_body_2,ELEMENT_rigid_body_4,ELEMENT_rigid_body_7,ELEMENT_rigid_body_10,ELEMENT_rigid_body_13,ELEMENT_rigid_body_22,ELEMENT_rigid_body_23]
  Origin = -> Origin020
FEATURE [App::MaterialObjectPython] ELEMENT_material_23  # material (typed FeaturePython)
  Category = 0
  Material = Density=7900.00 kg/m^3; Name=Steel-Generic
FEATURE [App::DocumentObjectGroupPython] MBD_materials  # scripted group (container) (typed FeaturePython)
  Group = -> [ELEMENT_material_1,ELEMENT_material_2,ELEMENT_material_4,ELEMENT_material_7,ELEMENT_material_10,ELEMENT_material_13,ELEMENT_material_22,ELEMENT_material_23]
FEATURE [PartDesign::CoordinateSystem] ELEMENT_structural_dynamic_23
  AttacherType = Attacher::AttachEngine3D
  Placement = pos=(-157.182,2.82038,38.9614) rot=(0,0,1;0rad)
  absolute_angular_velocity_X = 0
  absolute_angular_velocity_Y = 0
  absolute_angular_velocity_Z = 0
  absolute_orientation_matrix = 3, 0.0, 0.0, 1.0, 2, 0.0, 1.0, 0.0
  absolute_position_X = -157.182
  absolute_position_Y = 2.82038
  absolute_position_Z = 38.9614
  absolute_velocity_X = 0
  absolute_velocity_Y = 0
  absolute_velocity_Z = 0
  base_entity = -> ELEMENT_rigid_body_23
  initial_conditions_reference_system_angular_velocity = 0
  initial_conditions_reference_system_velocity = 0
  label = 23
  offset_pitch = 0
  offset_reference_system_orientation = 0
  offset_reference_system_position = 0
  offset_roll = 0
  offset_x = 0
  offset_y = 0
  offset_yaw = 0
  offset_z = 0
  placement_method = 1
  plugin_variables = none
  position_reference_1 = -> ELEMENT_rigid_body_23
  type = dynamic
FEATURE [App::DocumentObjectGroupPython] MBD_structural_dynamic_nodes  # scripted group (container) (typed FeaturePython)
  Group = -> [ELEMENT_structural_dynamic_1,ELEMENT_structural_dynamic_2,ELEMENT_structural_dynamic_4,ELEMENT_structural_dynamic_7,ELEMENT_structural_dynamic_10,ELEMENT_structural_dynamic_13,ELEMENT_structural_dynamic_22,ELEMENT_structural_dynamic_23]
FEATURE [PartDesign::CoordinateSystem] ELEMENT_structural_dummy_24
  AttacherType = Attacher::AttachEngine3D
  Placement = pos=(-117.45,3.09944e-06,56) rot=(0,0,1;0rad)
  absolute_position_X = -117.45
  absolute_position_Y = 3.09944e-06
  absolute_position_Z = 56
  base_entity = -> ELEMENT_rigid_body_4
  dummy_node_type = 0
  label = 24
  offset_pitch = 0
  offset_reference_system_orientation = 0
  offset_reference_system_position = 0
  offset_roll = 0
  offset_x = -10
  offset_y = 0
  offset_yaw = 0
  offset_z = 0
  placement_method = 1
  plugin_variables = "X_3_24": position in global direction 3 \n"XP_3_24": velocity in global direction 3
  position_reference_1 = -> ELEMENT_rigid_body_4 [Edge54]
  relative_offset_X = -38.0782
  relative_offset_Y = -2.9e-15
  relative_offset_Z = -25
  relative_orientation_matrix = 3, 0.0, 0.0, 1.0, 2, 0.0, 1.0, 0.0
  type = dummy
FEATURE [PartDesign::CoordinateSystem] ELEMENT_structural_dummy_26
  AttacherType = Attacher::AttachEngine3D
  Placement = pos=(-89.45,1.00001,118) rot=(0,0,1;0rad)
  absolute_position_X = -89.45
  absolute_position_Y = 1.00001
  absolute_position_Z = 118
  base_entity = -> ELEMENT_rigid_body_7
  dummy_node_type = 0
  label = 26
  offset_pitch = 0
  offset_reference_system_orientation = 0
  offset_reference_system_position = 0
  offset_roll = 0
  offset_x = 0
  offset_y = 0
  offset_yaw = 0
  offset_z = -3
  placement_method = 1
  plugin_variables = "X_3_26": position in global direction 3 \n"XP_3_26": velocity in global direction 3
  position_reference_1 = -> ELEMENT_rigid_body_7 [Face17]
  relative_offset_X = -3.07818
  relative_offset_Y = -4e-16
  relative_offset_Z = -28
  relative_orientation_matrix = 3, 0.0, 0.0, 1.0, 2, 0.0, 1.0, 0.0
  type = dummy
FEATURE [PartDesign::CoordinateSystem] ELEMENT_marker_7_4
  AttacherType = Attacher::AttachEngine3D
  Placement = pos=(-89.45,1.00001,121) rot=(0,-1,0;0.080285rad)
  base_entity = -> ELEMENT_rigid_body_7
  label = 7
  offset_pitch = 0
  offset_reference_system_orientation = 0
  offset_reference_system_position = 0
  offset_roll = 0
  offset_x = 0
  offset_y = 0
  offset_yaw = 0
  offset_z = 0
  placement_method = 1
  position_reference_1 = -> ELEMENT_rigid_body_7 [Face17]
FEATURE [App::DocumentObjectGroupPython] MBD_markers  # scripted group (container) (typed FeaturePython)
  Group = -> [ELEMENT_marker_2_1,ELEMENT_marker_2_2,ELEMENT_marker_1_1,ELEMENT_marker_4_1,ELEMENT_marker_4_2,ELEMENT_marker_7_1,ELEMENT_marker_7_2,ELEMENT_marker_10_1,ELEMENT_marker_10_3,ELEMENT_marker_13_1,ELEMENT_marker_13_2,ELEMENT_marker_13_3,ELEMENT_marker_13_4,ELEMENT_marker_10_004,ELEMENT_marker_7_3,ELEMENT_marker_2_3,ELEMENT_marker_7_4]
FEATURE [PartDesign::CoordinateSystem] ELEMENT_structural_internal_force_11
  AttacherType = Attacher::AttachEngine3D
  Placement = pos=(-55,3.09944e-06,110) rot=(0.999194,0,0.040132;3.14159rad)
  action_entity = -> ELEMENT_marker_7_4
  base_entity = -> ELEMENT_rigid_body_4
  contact_damping_activation_depth = 1e-06
  contact_damping_coefficient = 300
  contact_direction = 0
  contact_model = 1
  contact_offset = 0
  contact_stiffness_coefficient = 100000
  contact_stiffness_exponent = 1.2
  contact_type = 0
  direction = 0.08019892432885893, -1.2246467991473535e-16, -0.9967788784562475
  driven_element_expression = Time <= 1.0
  element_activation = 0
  force = structural internal force
  force_value = max(0, -Kc_11*(X_3_26 - X_3_8 + 0.0) - Cc_11*(XP_3_26 - XP_3_8))
  label = 11
  offset_pitch = -4.6
  offset_reference_system_orientation = 0
  offset_reference_system_position = 0
  offset_roll = 180
  offset_x = 0
  offset_y = 0
  offset_yaw = 0
  offset_z = 0
  placement_method = 1
  position_reference_1 = -> ELEMENT_rigid_body_4 [Edge15]
  reference_node_1 = 8
  reference_node_2 = 26
  relative_arm_1 = 0.06437180281637728, -3.0994324169841495e-09, 0.028999998109301785
  relative_arm_2 = -0.0030781825082684547, -4.440892098500626e-19, -0.024999999730896717
  type = 1
FEATURE [App::DocumentObjectGroupPython] MBD_structural_force_elements  # scripted group (container) (typed FeaturePython)
  Group = -> [ELEMENT_structural_force_1,ELEMENT_structural_internal_force_2,ELEMENT_structural_internal_force_3,ELEMENT_structural_internal_force_4,ELEMENT_structural_internal_force_5,ELEMENT_structural_internal_force_6,ELEMENT_structural_internal_force_7,ELEMENT_structural_internal_force_8,ELEMENT_structural_internal_force_9,ELEMENT_structural_internal_force_11]
FEATURE [App::DocumentObjectGroupPython] MBD_elements  # scripted group (container) (typed FeaturePython)
  Group = -> [MBD_beam_elements,MBD_body_elements,MBD_genel_elements,MBD_gravity_elements,MBD_hydraulic_elements,MBD_joint_elements,MBD_structural_couple_elements,MBD_structural_force_elements]
FEATURE [PartDesign::CoordinateSystem] ELEMENT_structural_dummy_25
  AttacherType = Attacher::AttachEngine3D
  Placement = pos=(-171,1.25005,46.5) rot=(0,0,1;0rad)
  absolute_position_X = -171
  absolute_position_Y = 1.25005
  absolute_position_Z = 46.5
  base_entity = -> ELEMENT_rigid_body_23
  dummy_node_type = 0
  label = 25
  offset_pitch = 0
  offset_reference_system_orientation = 0
  offset_reference_system_position = 0
  offset_roll = 0
  offset_x = 0
  offset_y = 0
  offset_yaw = 0
  offset_z = 0
  placement_method = 1
  plugin_variables = "X_3_25": position in global direction 3 \n"XP_3_25": velocity in global direction 3
  position_reference_1 = -> ELEMENT_rigid_body_23 [Edge6]
  relative_offset_X = -13.8182
  relative_offset_Y = -1.57034
  relative_offset_Z = 7.53861
  relative_orientation_matrix = 3, 0.0, 0.0, 1.0, 2, 0.0, 1.0, 0.0
  type = dummy
FEATURE [App::DocumentObjectGroupPython] MBD_structural_dummy_nodes  # scripted group (container) (typed FeaturePython)
  Group = -> [ELEMENT_structural_dummy_3,ELEMENT_structural_dummy_5,ELEMENT_structural_dummy_6,ELEMENT_structural_dummy_8,ELEMENT_structural_dummy_9,ELEMENT_structural_dummy_11,ELEMENT_structural_dummy_12,ELEMENT_structural_dummy_14,ELEMENT_structural_dummy_15,ELEMENT_structural_dummy_16,ELEMENT_structural_dummy_17,ELEMENT_structural_dummy_18,ELEMENT_structural_dummy_19,ELEMENT_structural_dummy_20,+4 more]
FEATURE [App::DocumentObjectGroupPython] MBD_nodes  # scripted group (container) (typed FeaturePython)
  Group = -> [MBD_abstract_nodes,MBD_structural_dummy_nodes,MBD_structural_dynamic_nodes,MBD_hydraulic_nodes,MBD_structural_static_nodes]
FEATURE [App::DocumentObjectGroupPython] MBD_simulation  # scripted group (container) (typed FeaturePython)
  Group = -> [MBD_animated_vectors,MBD_constitutive_laws,MBD_drives_and_drive_callers,MBD_global_reference_frame,MBD_input_files,MBD_materials,MBD_markers,MBD_nodes,MBD_elements,MBD_simulation_parameters,MBD_scalar_functions,MBD_user_defined_variables]

RESOLVED EXTERNAL PARTS (link-assembly join: the EXTERNAL_REF files above that resolve inside this repo's crawl, each included once):
---- part Stopper.FCStd = doc fcstd_0ad7f0afed72 ----
FCSTD DOCUMENT  (FreeCAD 0.22R35966 (Git))
Label: Stopper
License: All rights reserved
LicenseURL: http://en.wikipedia.org/wiki/All_rights_reserved
objects: Part::Box×1, Part::Cylinder×1, Part::MultiFuse×1, App::Part×1
note: 3 computed .brp shape members not serialized (recipe doc carries the construction recipe); baked Part::Feature solids carry a one-line shape summary decoded from their .brp

FEATURE [Part::Box] Box  label="Cube"
  AttacherType = Attacher::AttachEngine3D
  Height = 25
  Length = 45.5
  Placement = pos=(1e-15,-3,30) rot=(0,0,1;0rad)
  Width = 14.5
FEATURE [Part::Cylinder] Cylinder
  Angle = 360
  AttacherType = Attacher::AttachEngine3D
  FirstAngle = 0
  Height = 55
  Radius = 3
  SecondAngle = 0
FEATURE [Part::MultiFuse] Fusion
  Shapes = -> [Box,Cylinder]
FEATURE [App::Part] Part  label="Stopper"
  Group = -> [Cylinder,Box,Fusion]
  Origin = -> Origin
---- part pocketqube.FCStd = doc fcstd_475161709109 ----
FCSTD DOCUMENT  (FreeCAD 0.22R35966 (Git))
Label: pocketqube
License: All rights reserved
LicenseURL: http://en.wikipedia.org/wiki/All_rights_reserved
objects: Sketcher::SketchObject×1, PartDesign::Pad×1, PartDesign::Mirrored×1, PartDesign::Body×1, Part::Box×1, Part::MultiFuse×1, App::Part×1
note: 7 computed .brp shape members not serialized (recipe doc carries the construction recipe); baked Part::Feature solids carry a one-line shape summary decoded from their .brp

FEATURE [Sketcher::SketchObject] Sketch
  FullyConstrained = true
  MapMode = 5
  Support = -> [XY_Plane]
  sketch-geometry (8):
    g0: LineSegment StartX=-2.45 StartY=27 StartZ=0 EndX=-0.95 EndY=27 EndZ=0
    g1: LineSegment StartX=-0.95 StartY=27 StartZ=0 EndX=-0.95 EndY=29 EndZ=0
    g2: LineSegment StartX=-0.95 StartY=29 StartZ=0 EndX=0.95 EndY=29 EndZ=0
    g3: LineSegment StartX=0.95 StartY=29 StartZ=0 EndX=0.95 EndY=27 EndZ=0
    g4: LineSegment StartX=0.95 StartY=27 StartZ=0 EndX=2.45 EndY=27 EndZ=0
    g5: LineSegment StartX=2.45 StartY=27 StartZ=0 EndX=2.45 EndY=0 EndZ=0
    g6: LineSegment StartX=-2.45 StartY=27 StartZ=0 EndX=-2.45 EndY=0 EndZ=0
    g7: LineSegment StartX=-2.45 StartY=0 StartZ=0 EndX=2.45 EndY=0 EndZ=0
  constraints (23):
    c: Horizontal(g0)
    c: Coincident(g0,g1)
    c: Vertical(g1)
    c: Coincident(g1,g2)
    c: Coincident(g2,g3)
    c: Vertical(g3)
    c: Coincident(g3,g4)
    c: Horizontal(g4)
    c: Equal(g1,g3)
    c: Distance(g2,g2) = 1.9
    c: Equal(g0,g4)
    c: Symmetric(g1,g2,g-2)
    c: Distance(g1,g1) = 2
    c: DistanceX(g4,g4) = 1.5
    c: Coincident(g5,g4)
    c: Vertical(g5)
    c: PointOnObject(g5,g-1)
    c: DistanceY(g5,g5) = 27
    c: Coincident(g6,g0)
    c: PointOnObject(g6,g-1)
    c: Vertical(g6)
    c: Coincident(g7,g6)
    c: Coincident(g7,g5)
FEATURE [PartDesign::Pad] Pad
  Direction = (0,0,1)
  Length = 58
  Length2 = 10
  Midplane = true
  Profile = -> Sketch
  ReferenceAxis = -> Sketch [N_Axis]
  Suppressed = false
  Type = 0
FEATURE [PartDesign::Mirrored] Mirrored
  BaseFeature = -> Pad
  MirrorPlane = -> XZ_Plane
  Originals = -> [Pad]
  Suppressed = false
FEATURE [PartDesign::Body] Body
  Group = -> [Sketch,Pad,Mirrored]
  Origin = -> Origin
  Tip = -> Mirrored
FEATURE [Part::Box] Box  label="Cube"
  AttacherType = Attacher::AttachEngine3D
  Height = 50
  Length = 50
  Placement = pos=(2.45,-25,-25) rot=(0,0,1;0rad)
  Width = 50
FEATURE [Part::MultiFuse] Fusion
  Shapes = -> [Body,Box]
FEATURE [App::Part] Part  label="Satellite"
  Group = -> [Box,Body,Fusion]
  Origin = -> Origin001
---- part pusher.FCStd = doc fcstd_67d0559eb981 ----
FCSTD DOCUMENT  (FreeCAD 0.22R35966 (Git))
Label: pusher
License: All rights reserved
LicenseURL: http://en.wikipedia.org/wiki/All_rights_reserved
objects: Sketcher::SketchObject×9, TechDraw::DrawViewDimension×9, PartDesign::Pocket×6, TechDraw::DrawProjGroupItem×3, PartDesign::Pad×2, PartDesign::Plane×2, PartDesign::Body×2, App::Part×2, Spreadsheet::Sheet×1, TechDraw::DrawProjGroup×1, TechDraw::DrawViewPart×1, TechDraw::DrawViewAnnotation×1, TechDraw::DrawViewSection×1, TechDraw::DrawViewSymbol×1, TechDraw::DrawSVGTemplate×1, TechDraw::DrawPage×1
note: 29 computed .brp shape members not serialized (recipe doc carries the construction recipe); baked Part::Feature solids carry a one-line shape summary decoded from their .brp

FEATURE [Spreadsheet::Sheet] Spreadsheet  label="dim"
  cells = A2='Rail Height; B2(railHeight)=2; A3='Spring OD; B3(springOD)=40; A4='Rail from floor; B4(railFromFloor)=10; A5='Spring ID; B5(springID)=36; A6='spring Width; B6(springWidth)=20; A7='cylinder Width; B7(cylinderWidth)==springWidth + 8; A8='Rail Width; B8(railWidth)=58; A9='Rail top; B9(railTop)=1.5; A10='Axis OD; B10(axisOD)=6; A11='pilar Width; B11(pilarWidth)=6; A12='Rail Depth; B12(RailDepth)=2; A13='RBF OD; B13(RBFOD)=6; A14='RBF Seating D; B14(RBFSeatingD)=10; A15='RBF From Sat; B15(RBFFromSat)=7.5; A16='RBF From Rail; B16(RBFFromRail)=6.5
FEATURE [Sketcher::SketchObject] Sketch001
  FullyConstrained = false
  MapMode = 5
  Placement = pos=(0,0,0) rot=(0.57735,0.57735,0.57735;2.0944rad)
  Support = -> [YZ_Plane]
  expr: Constraints[10] = Sketch.Constraints[10]
  expr: Constraints[11] = Sketch.Constraints[11]
  expr: Constraints[12] = Sketch.Constraints[12]
  expr: Constraints[13] = Sketch.Constraints[13]
  expr: Constraints[16] = Sketch.Constraints[16]
  expr: Constraints[9] = Sketch.Constraints[9]
  sketch-geometry (21):
    g0: LineSegment StartX=-43.3303 StartY=12 StartZ=0 EndX=0 EndY=12 EndZ=0
    g1: LineSegment StartX=0 StartY=12 StartZ=0 EndX=0 EndY=10 EndZ=0
    g2: LineSegment StartX=0 StartY=10 StartZ=0 EndX=-43.3303 EndY=10 EndZ=0
    g3: LineSegment StartX=-43.3303 StartY=10 StartZ=0 EndX=-43.3303 EndY=12 EndZ=0
    g4: Circle CenterX=-25 CenterY=20 CenterZ=0 NormalX=0 NormalY=0 NormalZ=1 AngleXU=0 Radius=20
    g5: Circle CenterX=-25 CenterY=20 CenterZ=0 NormalX=0 NormalY=0 NormalZ=1 AngleXU=0 Radius=18
    g6: Circle CenterX=-25 CenterY=20 CenterZ=0 NormalX=0 NormalY=0 NormalZ=1 AngleXU=0 Radius=20
    g7: Circle CenterX=-25 CenterY=20 CenterZ=0 NormalX=0 NormalY=0 NormalZ=1 AngleXU=0 Radius=3
    g8: LineSegment StartX=-19.75 StartY=29.0933 StartZ=0 EndX=-30.25 EndY=29.0933 EndZ=0
    g9: LineSegment StartX=-30.25 StartY=29.0933 StartZ=0 EndX=-35.5 EndY=20 EndZ=0
    g10: LineSegment StartX=-35.5 StartY=20 StartZ=0 EndX=-30.25 EndY=10.9067 EndZ=0
    g11: LineSegment StartX=-30.25 StartY=10.9067 StartZ=0 EndX=-19.75 EndY=10.9067 EndZ=0
    g12: LineSegment StartX=-19.75 StartY=10.9067 StartZ=0 EndX=-14.5 EndY=20 EndZ=0
    g13: LineSegment StartX=-14.5 StartY=20 StartZ=0 EndX=-19.75 EndY=29.0933 EndZ=0
    g14: Circle CenterX=-25 CenterY=20 CenterZ=0 NormalX=0 NormalY=0 NormalZ=1 AngleXU=0 Radius=10.5
    g15: Circle CenterX=-19.75 CenterY=29.0933 CenterZ=0 NormalX=0 NormalY=0 NormalZ=1 AngleXU=0 Radius=5
    g16: Circle CenterX=-14.5 CenterY=20 CenterZ=0 NormalX=0 NormalY=0 NormalZ=1 AngleXU=0 Radius=4
    g17: Circle CenterX=-19.75 CenterY=10.9067 CenterZ=0 NormalX=0 NormalY=0 NormalZ=1 AngleXU=0 Radius=5
    g18: Circle CenterX=-30.25 CenterY=10.9067 CenterZ=0 NormalX=0 NormalY=0 NormalZ=1 AngleXU=0 Radius=4
    g19: Circle CenterX=-35.5 CenterY=20 CenterZ=0 NormalX=0 NormalY=0 NormalZ=1 AngleXU=0 Radius=5
    g20: Circle CenterX=-30.25 CenterY=29.0933 CenterZ=0 NormalX=0 NormalY=0 NormalZ=1 AngleXU=0 Radius=4
  constraints (49):
    c: Coincident(g0,g1)
    c: Coincident(g1,g2)
    c: Coincident(g2,g3)
    c: Coincident(g3,g0)
    c: Horizontal(g0)
    c: Horizontal(g2)
    c: Vertical(g1)
    c: Vertical(g3)
    c: PointOnObject(g0,g-2)
    c: Diameter(g4) = 40
    c: DistanceY(g-1,g4) = 20
    c: DistanceX(g4,g-1) = 25
    c: DistanceY(g1,g1) = 2
    c: DistanceY(g-1,g1) = 10
    c: PointOnObject(g0,g4)
    c: Coincident(g5,g4)
    c: Diameter(g5) = 36
    c: Coincident(g6,g4)
    c: Equal(g6,g4)
    c: Coincident(g7,g6)
    c: Diameter(g7) = 6
    c: Coincident(g8,g9)
    c: Coincident(g9,g10)
    c: Coincident(g10,g11)
    c: Coincident(g11,g12)
    c: Coincident(g12,g13)
    c: Coincident(g13,g8)
    c: Equal(g8, g9-g13) x5
    c: PointOnObject(g8,g14)
    c: PointOnObject(g9,g14)
    c: PointOnObject(g10,g14)
    c: PointOnObject(g11,g14)
    c: PointOnObject(g12,g14)
    c: PointOnObject(g13,g14)
    c: Horizontal(g8)
    c: Coincident(g14,g6)
    c: Coincident(g15,g8)
    c: Coincident(g16,g12)
    c: Coincident(g17,g11)
    c: Coincident(g18,g10)
    c: Coincident(g19,g9)
    c: Coincident(g20,g8)
    c: Diameter(g20) = 8
    c: Equal(g20,g16)
    c: Equal(g20,g18)
    c: Diameter(g15) = 10
    c: Equal(g15,g17)
    c: Equal(g15,g19)
    c: Diameter(g14) = 21
FEATURE [PartDesign::Pad] Pad
  AllowMultiFace = false
  Direction = (1,1,1)
  Length = 28
  Length2 = 100
  Midplane = true
  Placement = pos=(0,0,0) rot=(0.57735,0.57735,0.57735;2.0944rad)
  Profile = -> Sketch001
  Suppressed = false
  Type = 0
  expr: Length = <<dim>>.cylinderWidth
FEATURE [Sketcher::SketchObject] Sketch002
  FullyConstrained = false
  MapMode = 5
  Placement = pos=(0,0,0) rot=(0.57735,0.57735,0.57735;2.0944rad)
  Support = -> [YZ_Plane]
  expr: Constraints[10] = Sketch.Constraints[10]
  expr: Constraints[11] = Sketch.Constraints[11]
  expr: Constraints[12] = Sketch.Constraints[12]
  expr: Constraints[13] = Sketch.Constraints[13]
  expr: Constraints[16] = Sketch.Constraints[16]
  expr: Constraints[9] = Sketch.Constraints[9]
  sketch-geometry (6):
    g0: LineSegment StartX=-43.3303 StartY=12 StartZ=0 EndX=0 EndY=12 EndZ=0
    g1: LineSegment StartX=0 StartY=12 StartZ=0 EndX=0 EndY=10 EndZ=0
    g2: LineSegment StartX=0 StartY=10 StartZ=0 EndX=-43.3303 EndY=10 EndZ=0
    g3: LineSegment StartX=-43.3303 StartY=10 StartZ=0 EndX=-43.3303 EndY=12 EndZ=0
    g4: Circle CenterX=-25 CenterY=20 CenterZ=0 NormalX=0 NormalY=0 NormalZ=1 AngleXU=0 Radius=20
    g5: Circle CenterX=-25 CenterY=20 CenterZ=0 NormalX=0 NormalY=0 NormalZ=1 AngleXU=0 Radius=18
  constraints (17):
    c: Coincident(g0,g1)
    c: Coincident(g1,g2)
    c: Coincident(g2,g3)
    c: Coincident(g3,g0)
    c: Horizontal(g0)
    c: Horizontal(g2)
    c: Vertical(g1)
    c: Vertical(g3)
    c: PointOnObject(g0,g-2)
    c: Diameter(g4) = 40
    c: DistanceY(g-1,g4) = 20
    c: DistanceX(g4,g-1) = 25
    c: DistanceY(g1,g1) = 2
    c: DistanceY(g-1,g1) = 10
    c: PointOnObject(g0,g4)
    c: Coincident(g5,g4)
    c: Diameter(g5) = 36
FEATURE [PartDesign::Pocket] Pocket
  AllowMultiFace = false
  BaseFeature = -> Pad
  Direction = (1,1,1)
  Length = 20
  Length2 = 100
  Midplane = true
  Placement = pos=(0,0,0) rot=(0.57735,0.57735,0.57735;2.0944rad)
  Profile = -> Sketch002
  Suppressed = false
  Type = 0
  expr: Length = <<dim>>.springWidth
FEATURE [Sketcher::SketchObject] Sketch003
  FullyConstrained = false
  MapMode = 5
  Placement = pos=(0,0,0) rot=(1,0,0;1.5708rad)
  Support = -> [XZ_Plane001]
  expr: Constraints[31] = <<dim>>.railFromFloor
  expr: Constraints[37] = <<dim>>.railHeight - 0.1
  expr: Constraints[44] = <<dim>>.railWidth
  expr: Constraints[45] = <<dim>>.RailDepth
  sketch-geometry (20):
    g0: LineSegment StartX=27 StartY=8.5 StartZ=0 EndX=27 EndY=10 EndZ=0
    g1: LineSegment StartX=27 StartY=10 StartZ=0 EndX=29 EndY=10 EndZ=0
    g2: LineSegment StartX=29 StartY=10 StartZ=0 EndX=29 EndY=11.9 EndZ=0
    g3: LineSegment StartX=29 StartY=11.9 StartZ=0 EndX=27 EndY=11.9 EndZ=0
    g4: LineSegment StartX=27 StartY=11.9 StartZ=0 EndX=27 EndY=13.4 EndZ=0
    g5: LineSegment StartX=27 StartY=13.4 StartZ=0 EndX=26 EndY=13.4 EndZ=0
    g6: LineSegment StartX=24.0797 StartY=14.8411 StartZ=0 EndX=20.25 EndY=28 EndZ=0
    g7: LineSegment StartX=20.25 StartY=28 StartZ=0 EndX=14.25 EndY=28 EndZ=0
    g8: LineSegment StartX=-27 StartY=8.5 StartZ=0 EndX=-27 EndY=10 EndZ=0
    g9: LineSegment StartX=-27 StartY=10 StartZ=0 EndX=-29 EndY=10 EndZ=0
    g10: LineSegment StartX=-29 StartY=10 StartZ=0 EndX=-29 EndY=11.9 EndZ=0
    g11: LineSegment StartX=-29 StartY=11.9 StartZ=0 EndX=-27 EndY=11.9 EndZ=0
    g12: LineSegment StartX=-27 StartY=11.9 StartZ=0 EndX=-27 EndY=13.4 EndZ=0
    g13: LineSegment StartX=-27 StartY=13.4 StartZ=0 EndX=-26 EndY=13.4 EndZ=0
    g14: LineSegment StartX=-24.0797 StartY=14.8411 StartZ=0 EndX=-20.25 EndY=28 EndZ=0
    g15: LineSegment StartX=-20.25 StartY=28 StartZ=0 EndX=-14.25 EndY=28 EndZ=0
    g16: LineSegment StartX=14.25 StartY=28 StartZ=0 EndX=-14.25 EndY=28 EndZ=0
    g17: LineSegment StartX=-27 StartY=8.5 StartZ=0 EndX=27 EndY=8.5 EndZ=0
    g18: ArcOfCircle CenterX=-26 CenterY=15.4 CenterZ=0 NormalX=0 NormalY=0 NormalZ=1 AngleXU=0 Radius=2 StartAngle=4.71239 EndAngle=5.99997
    g19: ArcOfCircle CenterX=26 CenterY=15.4 CenterZ=0 NormalX=0 NormalY=0 NormalZ=1 AngleXU=0 Radius=2 StartAngle=3.4248 EndAngle=4.71239
  constraints (57):
    c: Vertical(g0)
    c: Coincident(g0,g1)
    c: Horizontal(g1)
    c: Coincident(g1,g2)
    c: Vertical(g2)
    c: Coincident(g2,g3)
    c: Horizontal(g3)
    c: Coincident(g3,g4)
    c: Coincident(g4,g5)
    c: Horizontal(g5)
    c: Coincident(g6,g7)
    c: Horizontal(g7)
    c: Vertical(g4)
    c: PointOnObject(g3,g0)
    c: Vertical(g8)
    c: Coincident(g8,g9)
    c: Horizontal(g9)
    c: Coincident(g9,g10)
    c: Vertical(g10)
    c: Coincident(g10,g11)
    c: Horizontal(g11)
    c: Coincident(g11,g12)
    c: Coincident(g12,g13)
    c: Horizontal(g13)
    c: Coincident(g14,g15)
    c: Horizontal(g15)
    c: Vertical(g12)
    c: PointOnObject(g11,g8)
    c: Coincident(g17,g8)
    c: Coincident(g17,g0)
    c: Symmetric(g8,g0,g-2)
    c: DistanceY(g-1,g9) = 10
    c: Equal(g8,g0)
    c: Equal(g9,g1)
    c: Equal(g2,g10)
    c: Equal(g12,g4)
    c: Equal(g5,g13)
    c: DistanceY(g10,g10) = 1.9
    c: Equal(g8,g12)
    c: DistanceY(g12,g12) = 1.5
    c: Equal(g15,g7)
    c: DistanceX(g16,g16) = 28.5
    c: DistanceY(g-1,g15) = 28  'pilarHeight'
    c: DistanceX(g15,g15) = 6
    c: DistanceX(g9,g1) = 58
    c: DistanceX(g1,g1) = 2
    c: Tangent(g14,g18) = -1.5708
    c: Tangent(g13,g18) = -1.5708
    c: Tangent(g6,g19) = 1.5708
    c: Tangent(g5,g19) = 1.5708
    c: Equal(g18,g19)
    c: Equal(g13,g5)
    c: Radius(g18) = 2
    c: DistanceX(g12,g18) = 1
    c: Coincident(g16,g15)
    c: Coincident(g16,g7)
    c: Symmetric(g7,g15,g-2)
FEATURE [PartDesign::Pad] Pad001
  AllowMultiFace = false
  Direction = (1,1,1)
  Length = 50
  Length2 = 100
  Placement = pos=(0,0,0) rot=(1,0,0;1.5708rad)
  Profile = -> Sketch003
  Suppressed = false
  Type = 0
FEATURE [Sketcher::SketchObject] Sketch004  label="baseSketch001"
  FullyConstrained = false
  MapMode = 5
  Placement = pos=(0,0,0) rot=(0.57735,0.57735,0.57735;2.0944rad)
  Support = -> [YZ_Plane001]
  expr: Constraints[18] = <<dim>>.axisOD
  expr: Constraints[36] = 10 + 1.9 + 1.5
  expr: Constraints[9] = <<dim>>.springOD
  sketch-geometry (19):
    g0: LineSegment StartX=-43.3303 StartY=12 StartZ=0 EndX=0 EndY=12 EndZ=0
    g1: LineSegment StartX=0 StartY=12 StartZ=0 EndX=0 EndY=10 EndZ=0
    g2: LineSegment StartX=0 StartY=10 StartZ=0 EndX=-43.3303 EndY=10 EndZ=0
    g3: LineSegment StartX=-43.3303 StartY=10 StartZ=0 EndX=-43.3303 EndY=12 EndZ=0
    g4: Circle CenterX=-25 CenterY=20 CenterZ=0 NormalX=0 NormalY=0 NormalZ=1 AngleXU=0 Radius=20
    g5: Circle CenterX=-25 CenterY=20 CenterZ=0 NormalX=0 NormalY=0 NormalZ=1 AngleXU=0 Radius=18
    g6: Circle CenterX=-25 CenterY=20 CenterZ=0 NormalX=0 NormalY=0 NormalZ=1 AngleXU=0 Radius=3
    g7: LineSegment StartX=-41.4553 StartY=18.2442 StartZ=0 EndX=-30.3662 EndY=24.9932 EndZ=0
    g8: LineSegment StartX=-17.5118 StartY=23.2798 StartZ=0 EndX=-12.821 EndY=18.3352 EndZ=0
    g9: LineSegment StartX=-1.33651 StartY=13.4 StartZ=0 EndX=5.50918 EndY=13.4 EndZ=0
    g10: LineSegment StartX=5.50918 StartY=13.4 StartZ=0 EndX=5.50918 EndY=39.591 EndZ=0
    g11: LineSegment StartX=5.50918 StartY=39.591 StartZ=0 EndX=-54.9003 EndY=39.591 EndZ=0
    g12: LineSegment StartX=-54.9003 StartY=39.591 StartZ=0 EndX=-54.9003 EndY=16.8241 EndZ=0
    g13: LineSegment StartX=-25 StartY=47.8975 StartZ=0 EndX=-25 EndY=-22.7529 EndZ=0
    g14: ArcOfCircle CenterX=-1.33651 CenterY=29.2301 CenterZ=0 NormalX=0 NormalY=0 NormalZ=1 AngleXU=0 Radius=15.8301 StartAngle=3.90065 EndAngle=4.71239
    g15: ArcOfCircle CenterX=-25 CenterY=16.176 CenterZ=0 NormalX=0 NormalY=0 NormalZ=1 AngleXU=0 Radius=10.3217 StartAngle=0.759059 EndAngle=2.11752
    g16: GeomPoint X=-25 Y=26.4977 Z=0
    g17: LineSegment StartX=-54.9003 StartY=16.8241 StartZ=0 EndX=-46.5205 EndY=16.8241 EndZ=0
    g18: ArcOfCircle CenterX=-46.5205 CenterY=26.5668 CenterZ=0 NormalX=0 NormalY=0 NormalZ=1 AngleXU=0 Radius=9.74273 StartAngle=4.71239 EndAngle=5.25911
  constraints (43):
    c: Coincident(g0,g1)
    c: Coincident(g1,g2)
    c: Coincident(g2,g3)
    c: Coincident(g3,g0)
    c: Horizontal(g0)
    c: Horizontal(g2)
    c: Vertical(g1)
    c: Vertical(g3)
    c: PointOnObject(g0,g-2)
    c: Diameter(g4) = 40
    c: DistanceY(g-1,g4) = 20  'H'
    c: DistanceX(g4,g-1) = 25  'centerFromBack'
    c: DistanceY(g1,g1) = 2
    c: DistanceY(g-1,g1) = 10
    c: PointOnObject(g0,g4)
    c: Coincident(g5,g4)
    c: Diameter(g5) = 36
    c: Coincident(g6,g4)
    c: Diameter(g6) = 6
    c: Horizontal(g9)
    c: Coincident(g9,g10)
    c: Vertical(g10)
    c: Coincident(g10,g11)
    c: Horizontal(g11)
    c: Coincident(g11,g12)
    c: Vertical(g12)
    c: PointOnObject(g6,g13)
    c: Tangent(g8,g14) = -1.5708
    c: Tangent(g9,g14) = -1.5708
    c: PointOnObject(g15,g13)
    c: Coincident(g15,g7)
    c: Coincident(g15,g8)
    c: Tangent(g7,g15) = 1.5708
    c: Tangent(g8,g15) = 1.5708
    c: PointOnObject(g16,g15)
    c: PointOnObject(g16,g13)
    c: DistanceY(g-1,g9) = 13.4
    c: Vertical(g13)
    c: Coincident(g17,g12)
    c: Coincident(g18,g7)
    c: Tangent(g7,g18) = -1.5708
    c: Horizontal(g17)
    c: Tangent(g17,g18) = -1.5708
FEATURE [PartDesign::Pocket] Pocket001
  AllowMultiFace = false
  BaseFeature = -> Pad001
  Direction = (1,1,1)
  Length = 5
  Length2 = 100
  Midplane = true
  Placement = pos=(0,0,0) rot=(1,0,0;1.5708rad)
  Profile = -> Sketch004
  Suppressed = false
  Type = 1
FEATURE [PartDesign::Plane] DatumPlane
  AttachmentOffset = pos=(0,0,28) rot=(0,0,1;0rad)
  Length = 71.1909
  MapMode = 3
  Placement = pos=(0,0,28) rot=(0,0,1;3.14159rad)
  ResizeMode = 0
  Support = -> [Pocket001]
  Width = 88.1909
FEATURE [Sketcher::SketchObject] Sketch005
  FullyConstrained = false
  MapMode = 5
  Placement = pos=(0,0,28) rot=(0,0,1;3.14159rad)
  Support = -> [DatumPlane]
  expr: Constraints[31] = <<dim>>.railWidth
  expr: Constraints[6] = Sketch004.Constraints.centerFromBack
  sketch-geometry (13):
    g0: LineSegment StartX=-29 StartY=32.75 StartZ=0 EndX=-23.5 EndY=32.75 EndZ=0
    g1: LineSegment StartX=-21.5 StartY=30.75 StartZ=0 EndX=-21.5 EndY=19.25 EndZ=0
    g2: LineSegment StartX=-23.5 StartY=17.25 StartZ=0 EndX=-29 EndY=17.25 EndZ=0
    g3: LineSegment StartX=-29 StartY=17.25 StartZ=0 EndX=-29 EndY=32.75 EndZ=0
    g4: LineSegment StartX=-29 StartY=25 StartZ=0 EndX=29 EndY=25 EndZ=0
    g5: ArcOfCircle CenterX=-23.5 CenterY=30.75 CenterZ=0 NormalX=0 NormalY=0 NormalZ=1 AngleXU=0 Radius=2 StartAngle=5e-16 EndAngle=1.5708
    g6: ArcOfCircle CenterX=-23.5 CenterY=19.25 CenterZ=0 NormalX=0 NormalY=0 NormalZ=1 AngleXU=0 Radius=2 StartAngle=4.71239 EndAngle=6.28319
    g7: LineSegment StartX=29 StartY=32.75 StartZ=0 EndX=23.5 EndY=32.75 EndZ=0
    g8: LineSegment StartX=21.5 StartY=30.75 StartZ=0 EndX=21.5 EndY=19.25 EndZ=0
    g9: LineSegment StartX=23.5 StartY=17.25 StartZ=0 EndX=29 EndY=17.25 EndZ=0
    g10: LineSegment StartX=29 StartY=17.25 StartZ=0 EndX=29 EndY=32.75 EndZ=0
    g11: ArcOfCircle CenterX=23.5 CenterY=30.75 CenterZ=0 NormalX=0 NormalY=0 NormalZ=1 AngleXU=0 Radius=2 StartAngle=1.5708 EndAngle=3.14159
    g12: ArcOfCircle CenterX=23.5 CenterY=19.25 CenterZ=0 NormalX=0 NormalY=0 NormalZ=1 AngleXU=0 Radius=2 StartAngle=3.14159 EndAngle=4.71239
  constraints (32):
    c: Coincident(g2,g3)
    c: Coincident(g3,g0)
    c: Horizontal(g0)
    c: Horizontal(g2)
    c: Vertical(g3)
    c: Horizontal(g4)
    c: DistanceY(g-1,g4) = 25
    c: Tangent(g1,g5) = 1.5708
    c: Tangent(g0,g5) = 1.5708
    c: Tangent(g1,g6) = 1.5708
    c: Tangent(g2,g6) = 1.5708
    c: Equal(g6,g5)
    c: Radius(g5) = 2
    c: Symmetric(g1,g1,g4)
    c: DistanceY(g1,g1) = 11.5
    c: Coincident(g9,g10)
    c: Coincident(g10,g7)
    c: Horizontal(g7)
    c: Horizontal(g9)
    c: Vertical(g10)
    c: Tangent(g8,g11) = -1.5708
    c: Tangent(g7,g11) = -1.5708
    c: Tangent(g8,g12) = -1.5708
    c: Tangent(g9,g12) = -1.5708
    c: Equal(g12,g11)
    c: Symmetric(g8,g1,g-2)
    c: DistanceX(g1,g8) = 43
    c: Symmetric(g8,g8,g4)
    c: PointOnObject(g4,g3)
    c: PointOnObject(g4,g10)
    c: Symmetric(g9,g2,g-2)
    c: DistanceX(g0,g7) = 58
FEATURE [PartDesign::Pocket] Pocket002
  AllowMultiFace = false
  BaseFeature = -> Pocket001
  Direction = (1,1,1)
  Length = 14.6
  Length2 = 100
  Placement = pos=(0,0,0) rot=(1,0,0;1.5708rad)
  Profile = -> Sketch005
  Suppressed = false
  Type = 0
FEATURE [Sketcher::SketchObject] Sketch006
  FullyConstrained = false
  MapMode = 5
  Support = -> [XY_Plane001]
  sketch-geometry (8):
    g0: LineSegment StartX=-12.3486 StartY=-4.73756 StartZ=0 EndX=12.3447 EndY=-4.73756 EndZ=0
    g1: LineSegment StartX=14.3447 StartY=-6.73756 StartZ=0 EndX=14.3447 EndY=-43.7105 EndZ=0
    g2: LineSegment StartX=12.3447 StartY=-45.7105 StartZ=0 EndX=-12.3486 EndY=-45.7105 EndZ=0
    g3: LineSegment StartX=-14.3486 StartY=-43.7105 StartZ=0 EndX=-14.3486 EndY=-6.73756 EndZ=0
    g4: ArcOfCircle CenterX=12.3447 CenterY=-6.73756 CenterZ=0 NormalX=0 NormalY=0 NormalZ=1 AngleXU=0 Radius=2 StartAngle=1e-16 EndAngle=1.5708
    g5: ArcOfCircle CenterX=-12.3486 CenterY=-6.73756 CenterZ=0 NormalX=0 NormalY=0 NormalZ=1 AngleXU=0 Radius=2 StartAngle=1.5708 EndAngle=3.14159
    g6: ArcOfCircle CenterX=-12.3486 CenterY=-43.7105 CenterZ=0 NormalX=0 NormalY=0 NormalZ=1 AngleXU=0 Radius=2 StartAngle=3.14159 EndAngle=4.71239
    g7: ArcOfCircle CenterX=12.3447 CenterY=-43.7105 CenterZ=0 NormalX=0 NormalY=0 NormalZ=1 AngleXU=0 Radius=2 StartAngle=4.71239 EndAngle=6.28319
  constraints (16):
    c: Horizontal(g0)
    c: Horizontal(g2)
    c: Vertical(g1)
    c: Vertical(g3)
    c: Tangent(g1,g4) = 1.5708
    c: Tangent(g0,g4) = 1.5708
    c: Tangent(g0,g5) = 1.5708
    c: Tangent(g3,g5) = 1.5708
    c: Tangent(g3,g6) = 1.5708
    c: Tangent(g2,g6) = 1.5708
    c: Tangent(g1,g7) = 1.5708
    c: Tangent(g2,g7) = 1.5708
    c: Equal(g4,g5)
    c: Equal(g5,g6)
    c: Equal(g6,g7)
    c: Radius(g4) = 2
FEATURE [PartDesign::Pocket] Pocket003
  AllowMultiFace = false
  BaseFeature = -> Pocket002
  Direction = (1,1,1)
  Length = 5
  Length2 = 100
  Midplane = true
  Placement = pos=(0,0,0) rot=(1,0,0;1.5708rad)
  Profile = -> Sketch006
  Reversed = true
  Suppressed = false
  Type = 1
FEATURE [PartDesign::Plane] DatumPlane001
  AttachmentOffset = pos=(0,0,18) rot=(0,0,1;0rad)
  Length = 71.1909
  MapMode = 5
  Placement = pos=(0,0,18) rot=(0,0,1;0rad)
  ResizeMode = 0
  Support = -> [XY_Plane001]
  Width = 88.1909
FEATURE [Sketcher::SketchObject] Sketch007
  FullyConstrained = false
  MapMode = 5
  Placement = pos=(0,0,18) rot=(0,0,1;0rad)
  Support = -> [DatumPlane001]
  expr: Constraints[0] = <<dim>>.RBFSeatingD
  expr: Constraints[1] = <<dim>>.RBFFromSat
  expr: Constraints[2] = <<dim>>.railWidth / 2 - <<dim>>.RailDepth - <<dim>>.RBFFromRail
  sketch-geometry (1):
    g0: Circle CenterX=-20.5 CenterY=-7.5 CenterZ=0 NormalX=0 NormalY=0 NormalZ=1 AngleXU=0 Radius=5
  constraints (3):
    c: Diameter(g0) = 10
    c: DistanceY(g0,g-1) = 7.5
    c: DistanceX(g0,g-1) = 20.5
FEATURE [PartDesign::Pocket] Pocket004
  AllowMultiFace = false
  BaseFeature = -> Pocket003
  Direction = (1,1,1)
  Length = 10
  Length2 = 100
  Midplane = true
  Placement = pos=(0,0,0) rot=(1,0,0;1.5708rad)
  Profile = -> Sketch007
  Suppressed = false
  Type = 0
FEATURE [Sketcher::SketchObject] Sketch008
  FullyConstrained = false
  MapMode = 5
  Placement = pos=(0,0,18) rot=(0,0,1;0rad)
  Support = -> [DatumPlane001]
  expr: Constraints[0] = <<dim>>.RBFOD
  expr: Constraints[1] = <<dim>>.RBFFromSat
  expr: Constraints[2] = <<dim>>.railWidth / 2 - <<dim>>.RailDepth - <<dim>>.RBFFromRail
  sketch-geometry (1):
    g0: Circle CenterX=-20.5 CenterY=-7.5 CenterZ=0 NormalX=0 NormalY=0 NormalZ=1 AngleXU=0 Radius=3
  constraints (3):
    c: Diameter(g0) = 6
    c: DistanceY(g0,g-1) = 7.5
    c: DistanceX(g0,g-1) = 20.5
FEATURE [PartDesign::Pocket] Pocket005
  AllowMultiFace = false
  BaseFeature = -> Pocket004
  Direction = (1,1,1)
  Length = 5
  Length2 = 100
  Placement = pos=(0,0,0) rot=(1,0,0;1.5708rad)
  Profile = -> Sketch008
  Suppressed = false
  Type = 1
FEATURE [Sketcher::SketchObject] Sketch  label="baseSketch"
  FullyConstrained = true
  MapMode = 5
  Placement = pos=(-21.5,0,0) rot=(0.707107,0,-0.707107;3.14159rad)
  Support = -> [Pocket005]
  expr: Constraints[10] = <<dim>>.springOD / 2
  expr: Constraints[11] = <<dim>>.springOD / 2 + 5
  expr: Constraints[12] = <<dim>>.railHeight
  expr: Constraints[13] = <<dim>>.railFromFloor
  expr: Constraints[16] = <<dim>>.springID
  expr: Constraints[9] = <<dim>>.springOD
  sketch-geometry (6):
    g0: LineSegment StartX=-43.3303 StartY=12 StartZ=0 EndX=0 EndY=12 EndZ=0
    g1: LineSegment StartX=0 StartY=12 StartZ=0 EndX=0 EndY=10 EndZ=0
    g2: LineSegment StartX=0 StartY=10 StartZ=0 EndX=-43.3303 EndY=10 EndZ=0
    g3: LineSegment StartX=-43.3303 StartY=10 StartZ=0 EndX=-43.3303 EndY=12 EndZ=0
    g4: Circle CenterX=-25 CenterY=20 CenterZ=0 NormalX=0 NormalY=0 NormalZ=1 AngleXU=0 Radius=20
    g5: Circle CenterX=-25 CenterY=20 CenterZ=0 NormalX=0 NormalY=0 NormalZ=1 AngleXU=0 Radius=18
  constraints (17):
    c: Coincident(g0,g1)
    c: Coincident(g1,g2)
    c: Coincident(g2,g3)
    c: Coincident(g3,g0)
    c: Horizontal(g0)
    c: Horizontal(g2)
    c: Vertical(g1)
    c: Vertical(g3)
    c: PointOnObject(g0,g-2)
    c: Diameter(g4) = 40
    c: DistanceY(g-1,g4) = 20
    c: DistanceX(g4,g-1) = 25
    c: DistanceY(g1,g1) = 2
    c: DistanceY(g-1,g1) = 10
    c: PointOnObject(g0,g4)
    c: Coincident(g5,g4)
    c: Diameter(g5) = 36
FEATURE [PartDesign::Body] Body  label="SpoolBody"
  Group = -> [Sketch,Sketch001,Pad,Sketch002,Pocket]
  Origin = -> Origin
  Tip = -> Pocket
FEATURE [PartDesign::Body] Body001  label="PusherBody"
  Group = -> [Sketch003,Pad001,Sketch004,Pocket001,DatumPlane,Sketch005,Pocket002,Sketch006,Pocket003,DatumPlane001,Sketch007,Pocket004,Sketch008,Pocket005]
  Origin = -> Origin001
  Tip = -> Pocket005
FEATURE [TechDraw::DrawProjGroupItem] ProjItem  label="Front"
  CoarseView = false
  Direction = (0,1,0)
  Focus = 100
  HardHidden = false
  IsoCount = 0
  IsoHidden = false
  IsoVisible = false
  LockPosition = true
  Perspective = false
  Rotation = 0
  RotationVector = (-1,0,2e-16)
  ScaleType = 2
  ScrubCount = 0
  SeamHidden = false
  SeamVisible = false
  SmoothHidden = false
  SmoothVisible = false
  Source = -> [Body001]
  Type = 0
  X = 0
  XDirection = (-1,0,2e-16)
  Y = 0
FEATURE [TechDraw::DrawViewDimension] Dimension
  AngleOverride = false
  Arbitrary = false
  ArbitraryTolerances = false
  EqualTolerance = false
  ExtensionAngle = 0
  FormatSpec = %.2f
  FormatSpecOverTolerance = %+.2w
  FormatSpecUnderTolerance = %+.2w
  Inverted = false
  LineAngle = 0
  LockPosition = false
  MeasureType = 1
  OverTolerance = 0
  References2D = -> [ProjItem]
  Rotation = 0
  ScaleType = 0
  TheoreticalExact = false
  Type = 2
  UnderTolerance = -0.1
  X = 36.6294
  Y = 6.67132
FEATURE [TechDraw::DrawViewDimension] Dimension002
  AngleOverride = false
  Arbitrary = false
  ArbitraryTolerances = false
  EqualTolerance = false
  ExtensionAngle = 0
  FormatSpec = %.2f
  FormatSpecOverTolerance = %+.2w
  FormatSpecUnderTolerance = %+.2w
  Inverted = false
  LineAngle = 0
  LockPosition = false
  MeasureType = 1
  OverTolerance = 0.2
  References2D = -> [ProjItem]
  Rotation = 0
  ScaleType = 0
  TheoreticalExact = false
  Type = 1
  UnderTolerance = 0
  X = -2.72566
  Y = -27.6367
FEATURE [TechDraw::DrawViewDimension] Dimension001
  AngleOverride = false
  Arbitrary = false
  ArbitraryTolerances = false
  EqualTolerance = false
  ExtensionAngle = 0
  FormatSpec = %.2f
  FormatSpecOverTolerance = %+.2w
  FormatSpecUnderTolerance = %+.2w
  Inverted = false
  LineAngle = 0
  LockPosition = false
  MeasureType = 1
  OverTolerance = 0
  References2D = -> [ProjItem]
  Rotation = 0
  ScaleType = 0
  TheoreticalExact = false
  Type = 1
  UnderTolerance = -0.1
  X = -1.94598
  Y = -18.3684
FEATURE [TechDraw::DrawProjGroupItem] ProjItem001  label="Top"
  CoarseView = false
  Direction = (2e-16,0,1)
  Focus = 100
  HardHidden = false
  IsoCount = 0
  IsoHidden = false
  IsoVisible = false
  LockPosition = false
  Perspective = false
  Rotation = 0
  RotationVector = (-1,0,2e-16)
  ScaleType = 2
  ScrubCount = 0
  SeamHidden = false
  SeamVisible = false
  SmoothHidden = false
  SmoothVisible = false
  Source = -> [Body001]
  Type = 4
  X = 0
  XDirection = (-1,0,2e-16)
  Y = -75.6668
FEATURE [TechDraw::DrawViewDimension] Dimension013
  AngleOverride = false
  Arbitrary = false
  ArbitraryTolerances = false
  EqualTolerance = false
  ExtensionAngle = 0
  FormatSpec = %.2f
  FormatSpecOverTolerance = %+.2w
  FormatSpecUnderTolerance = %+.2w
  Inverted = false
  LineAngle = 0
  LockPosition = false
  MeasureType = 1
  OverTolerance = 0
  References2D = -> [ProjItem001]
  Rotation = 0
  ScaleType = 0
  TheoreticalExact = false
  Type = 1
  UnderTolerance = -0.2
  X = 0.220775
  Y = 34.3046
FEATURE [TechDraw::DrawProjGroupItem] ProjItem002  label="Left"
  CoarseView = false
  Direction = (1,1e-16,-2e-16)
  Focus = 100
  HardHidden = false
  IsoCount = 0
  IsoHidden = false
  IsoVisible = false
  LockPosition = false
  Perspective = false
  Rotation = 0
  RotationVector = (-1e-16,1,0)
  ScaleType = 2
  ScrubCount = 0
  SeamHidden = false
  SeamVisible = false
  SmoothHidden = false
  SmoothVisible = false
  Source = -> [Body001]
  Type = 1
  X = 88.1389
  XDirection = (-1e-16,1,0)
  Y = 0
FEATURE [TechDraw::DrawProjGroup] ProjGroup
  Anchor = -> ProjItem
  AutoDistribute = false
  LockPosition = true
  ProjectionType = 1
  Rotation = 0
  ScaleType = 2
  Source = -> [Body001]
  Views = -> [ProjItem,ProjItem001,ProjItem002]
  X = 65.1601
  Y = 132.263
  spacingX = 50
  spacingY = 50
FEATURE [TechDraw::DrawViewPart] View
  CoarseView = false
  Direction = (-0.675,0.521,0.523)
  Focus = 100
  HardHidden = false
  IsoCount = 0
  IsoHidden = false
  IsoVisible = false
  LockPosition = true
  Perspective = false
  Rotation = 0
  ScaleType = 0
  ScrubCount = 0
  SeamHidden = false
  SeamVisible = false
  SmoothHidden = false
  SmoothVisible = false
  Source = -> [Body001]
  X = 245.336
  XDirection = (-0.611013,-0.79162,0)
  Y = 174.088
FEATURE [TechDraw::DrawViewAnnotation] Annotation  label="Notes"
  Font = DejaVu Sans
  LineSpace = 80
  LockPosition = true
  MaxWidth = -1
  Rotation = 0
  ScaleType = 0
  Text = Notes: | 1. Drill Hole \u23006.0 THRU | 2. Mating hole (H7) for part P/N: MISUMI GHCCG6-43, | Shaft Dia. D: 6, Tolerance: g6 (sliding fit) | 3. Material, PTFE | 4. This part is mating with part, P/N: Deployer - Rail
  TextSize = 4
  TextStyle = 0
  X = 65.3721
  Y = 185.184
FEATURE [TechDraw::DrawViewSection] DrawViewSection  label="Section A - A"
  BaseView = -> ProjItem001
  CoarseView = false
  CutSurfaceDisplay = 2
  Direction = (0,-1,0)
  FileGeomPattern = <path>
  Focus = 100
  FuseBeforeCut = true
  HardHidden = false
  HatchOffset = (0,0,0)
  HatchRotation = 0
  HatchScale = 1
  IsoCount = 0
  IsoHidden = false
  IsoVisible = false
  LockPosition = false
  NameGeomPattern = Diamond
  Perspective = false
  Rotation = 0
  ScaleType = 0
  ScrubCount = 0
  SeamHidden = false
  SeamVisible = false
  SectionDirection = 2
  SectionLineStretch = 1
  SectionNormal = (0,-1,0)
  SectionOrigin = (0,-25,17.5)
  SectionSymbol = A
  SmoothHidden = false
  SmoothVisible = false
  Source = -> [Body001]
  TrimAfterCut = false
  UsePreviousCut = false
  X = 239.047
  XDirection = (-1,0,2e-16)
  Y = 85.4975
FEATURE [TechDraw::DrawViewSymbol] Symbol
  LockPosition = false
  Rotation = 0
  ScaleType = 2
  Symbol = <blob: 3150 chars omitted>
  X = 259.119
  Y = 104.279
FEATURE [TechDraw::DrawSVGTemplate] Template
  EditableTexts = Designed_by_Name=Papamatthaiou M.; FC-Date=29/10/2019; FC-SC=1:1; FC-SHEET=1/1; FC-Title=PocketQube Pusher; MATERIAL=NOTE-3; REV=A; ROUGHNESS=-; Subtitle=pusher; TOLERANCES=DIN ISO 2768- mK; Weight=N/A
  Height = 210
  Orientation = 1
  Width = 297
FEATURE [TechDraw::DrawViewDimension] Dimension015
  AngleOverride = false
  Arbitrary = false
  ArbitraryTolerances = false
  EqualTolerance = false
  ExtensionAngle = 0
  FormatSpec = (Note-1) ⌀%.2f
  FormatSpecOverTolerance = %+.2w
  FormatSpecUnderTolerance = %+.2w
  Inverted = false
  LineAngle = 0
  LockPosition = false
  MeasureType = 1
  OverTolerance = 0
  References2D = -> [ProjItem001]
  Rotation = 0
  ScaleType = 0
  TheoreticalExact = false
  Type = 5
  UnderTolerance = 0
  X = 52.104
  Y = -9.97206
FEATURE [TechDraw::DrawViewDimension] Dimension016
  AngleOverride = false
  Arbitrary = false
  ArbitraryTolerances = false
  EqualTolerance = false
  ExtensionAngle = 0
  FormatSpec = %.2f
  FormatSpecOverTolerance = %+.2w
  FormatSpecUnderTolerance = %+.2w
  Inverted = false
  LineAngle = 0
  LockPosition = false
  MeasureType = 1
  OverTolerance = 0.1
  References2D = -> [ProjItem001]
  Rotation = 0
  ScaleType = 0
  TheoreticalExact = false
  Type = 1
  UnderTolerance = -0.1
  X = 48.8608
  Y = -29.8266
FEATURE [TechDraw::DrawViewDimension] Dimension017
  AngleOverride = false
  Arbitrary = false
  ArbitraryTolerances = false
  EqualTolerance = false
  ExtensionAngle = 0
  FormatSpec = %.2f
  FormatSpecOverTolerance = %+.2w
  FormatSpecUnderTolerance = %+.2w
  Inverted = false
  LineAngle = 0
  LockPosition = false
  MeasureType = 1
  OverTolerance = 0.1
  References2D = -> [ProjItem002]
  Rotation = 0
  ScaleType = 0
  TheoreticalExact = false
  Type = 2
  UnderTolerance = 0
  X = 35.9807
  Y = -22.5661
FEATURE [TechDraw::DrawViewDimension] Dimension018
  AngleOverride = false
  Arbitrary = false
  ArbitraryTolerances = false
  EqualTolerance = false
  ExtensionAngle = 0
  FormatSpec = %.2f
  FormatSpecOverTolerance = %+.2w
  FormatSpecUnderTolerance = %+.2w
  Inverted = false
  LineAngle = 0
  LockPosition = false
  MeasureType = 1
  OverTolerance = 0.1
  References2D = -> [ProjItem002]
  Rotation = 0
  ScaleType = 0
  TheoreticalExact = false
  Type = 1
  UnderTolerance = 0
  X = 13.9643
  Y = -27.3146
FEATURE [TechDraw::DrawViewDimension] Dimension019
  AngleOverride = false
  Arbitrary = false
  ArbitraryTolerances = false
  EqualTolerance = false
  ExtensionAngle = 0
  FormatSpec = (Note-2) ⌀%.2f
  FormatSpecOverTolerance = %+.2w
  FormatSpecUnderTolerance = %+.2w
  Inverted = false
  LineAngle = 0
  LockPosition = false
  MeasureType = 1
  OverTolerance = 0.01
  References2D = -> [ProjItem002]
  Rotation = 0
  ScaleType = 0
  TheoreticalExact = false
  Type = 5
  UnderTolerance = 0
  X = 26.4792
  Y = 20.6918
FEATURE [TechDraw::DrawPage] Page
  KeepUpdated = true
  NextBalloonIndex = 1
  ProjectionType = 0
  Template = -> Template
  Views = -> [ProjGroup,View,Dimension,Dimension001,Dimension002,Annotation,Dimension013,DrawViewSection,Symbol,Dimension015,Dimension016,Dimension017,Dimension018,Dimension019]
FEATURE [App::Part] Part  label="Pusher"
  Group = -> [Body001]
  Origin = -> Origin002
FEATURE [App::Part] Part001  label="Spool"
  Group = -> [Body]
  Origin = -> Origin003
note: 1 file-system path scrubbed to <path> (originals preserved in the JSON sidecar)
